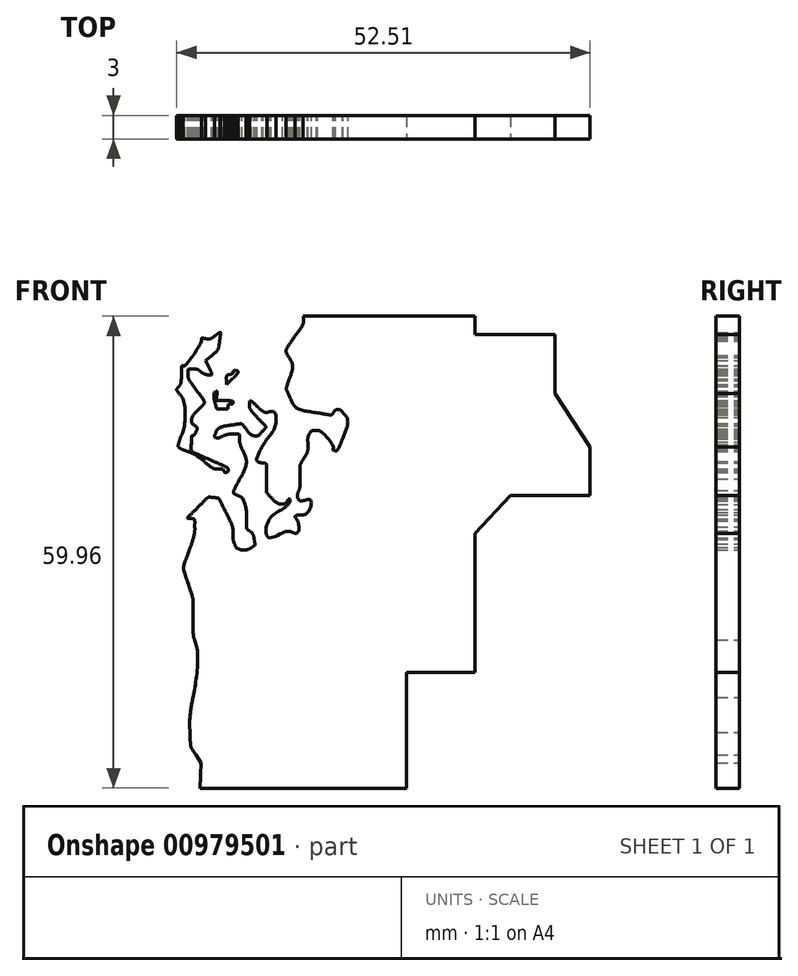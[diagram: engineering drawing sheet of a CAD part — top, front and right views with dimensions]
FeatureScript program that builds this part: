
annotation { "Feature Type Name" : "Feature", "Feature Type Description" : "" }
export const myFeature = defineFeature(function(context is Context, id is Id, definition is map)
    precondition{}
    {
        {
            var Q0;
            Q0=qCreatedBy(makeId("Front.planeOp"),FACE);
            var sketch = newSketch(context, id + "F0", { "sketchPlane" : qUnion([Q0])});
            skLineSegment(sketch, "E0", {"start": v(-32.88, 19.2) * mm, "end": v(-32.1, 20.83) * mm});
            skLineSegment(sketch, "E1", {"start": v(-32.1, 20.83) * mm, "end": v(-32.57, 22.16) * mm});
            skLineSegment(sketch, "E2", {"start": v(-27.5, 16.63) * mm, "end": v(-26.83, 16.28) * mm});
            skLineSegment(sketch, "E3", {"start": v(-26.83, 16.28) * mm, "end": v(-26.97, 16.83) * mm});
            skLineSegment(sketch, "E4", {"start": v(-24.85, 15.67) * mm, "end": v(-25.4, 15.88) * mm});
            skLineSegment(sketch, "E5", {"start": v(-25.4, 15.88) * mm, "end": v(-25.34, 18.4) * mm});
            skLineSegment(sketch, "E6", {"start": v(-1.75, 78.04) * mm, "end": v(-0.2, 79.6) * mm});
            skLineSegment(sketch, "E7", {"start": v(-0.2, 79.6) * mm, "end": v(1.27, 79.6) * mm});
            skLineSegment(sketch, "E8", {"start": v(38.3, 44.26) * mm, "end": v(38.3, 43.17) * mm});
            skLineSegment(sketch, "E9", {"start": v(38.3, 43.17) * mm, "end": v(37.62, 43.24) * mm});
            skLineSegment(sketch, "E10", {"start": v(39.65, -31.25) * mm, "end": v(39.52, -33.83) * mm});
            skLineSegment(sketch, "E11", {"start": v(39.52, -33.83) * mm, "end": v(40.18, -34.42) * mm});
            skLineSegment(sketch, "E12", {"start": v(1.4, 79.08) * mm, "end": v(0.3, 79.22) * mm});
            skLineSegment(sketch, "E13", {"start": v(0.3, 79.22) * mm, "end": v(-1.23, 77.67) * mm});
            skLineSegment(sketch, "E14", {"start": v(-12.51, 69.45) * mm, "end": v(-13.4, 69.45) * mm});
            skLineSegment(sketch, "E15", {"start": v(-13.4, 69.45) * mm, "end": v(-13.27, 67.07) * mm});
            skLineSegment(sketch, "E16", {"start": v(-18.31, 54.9) * mm, "end": v(-18.88, 53.48) * mm});
            skLineSegment(sketch, "E17", {"start": v(-18.88, 53.48) * mm, "end": v(-18.43, 53.1) * mm});
            skLineSegment(sketch, "E18", {"start": v(-20.94, 40.45) * mm, "end": v(-21.55, 40.45) * mm});
            skLineSegment(sketch, "E19", {"start": v(-21.55, 40.45) * mm, "end": v(-21.44, 41.8) * mm});
            skLineSegment(sketch, "E20", {"start": v(-24.47, 43.3) * mm, "end": v(-25.23, 42.61) * mm});
            skLineSegment(sketch, "E21", {"start": v(-25.23, 42.61) * mm, "end": v(-24.8, 41.05) * mm});
            skLineSegment(sketch, "E22", {"start": v(-37.96, -16.18) * mm, "end": v(-37.29, -17.23) * mm});
            skLineSegment(sketch, "E23", {"start": v(-37.29, -17.23) * mm, "end": v(-37.41, -20.41) * mm});
            skLineSegment(sketch, "E24", {"start": v(-30.4, -60.92) * mm, "end": v(-31.42, -62.04) * mm});
            skLineSegment(sketch, "E25", {"start": v(-31.42, -62.04) * mm, "end": v(-30.9, -63.02) * mm});
            skLineSegment(sketch, "E26", {"start": v(-36.35, 33.14) * mm, "end": v(-36.7, 33.88) * mm});
            skLineSegment(sketch, "E27", {"start": v(-36.7, 33.88) * mm, "end": v(-35.92, 34.57) * mm});
            skLineSegment(sketch, "E28", {"start": v(-34.09, 31.43) * mm, "end": v(-34.09, 30.84) * mm});
            skLineSegment(sketch, "E29", {"start": v(-34.09, 30.84) * mm, "end": v(-33.35, 31.56) * mm});
            skFitSpline(sketch, "E30", {"points": [v(-13.45, -80.7) * mm, v(-14.26, -80.4) * mm, v(-15.79, -79.86) * mm, v(-16.84, -79.51) * mm]});
            skFitSpline(sketch, "E31", {"points": [v(-16.84, -79.51) * mm, v(-20.43, -78.33) * mm, v(-20.6, -78.25) * mm, v(-21.55, -77.26) * mm]});
            skFitSpline(sketch, "E32", {"points": [v(-21.55, -77.26) * mm, v(-22.07, -76.72) * mm, v(-23.66, -74.52) * mm, v(-25.09, -72.37) * mm]});
            skFitSpline(sketch, "E33", {"points": [v(-25.09, -72.37) * mm, v(-26.52, -70.21) * mm, v(-28.36, -67.6) * mm, v(-29.19, -66.55) * mm]});
            skFitSpline(sketch, "E34", {"points": [v(-29.19, -66.55) * mm, v(-30.6, -64.76) * mm, v(-31.97, -62.53) * mm, v(-31.97, -62.03) * mm]});
            skFitSpline(sketch, "E35", {"points": [v(-31.97, -62.03) * mm, v(-31.97, -61.91) * mm, v(-31.5, -61.27) * mm, v(-30.92, -60.6) * mm]});
            skFitSpline(sketch, "E36", {"points": [v(-30.92, -60.6) * mm, v(-29.85, -59.39) * mm, v(-29, -57.92) * mm, v(-29, -57.28) * mm]});
            skFitSpline(sketch, "E37", {"points": [v(-29, -57.28) * mm, v(-29, -57.08) * mm, v(-29.34, -56.3) * mm, v(-29.75, -55.53) * mm]});
            skFitSpline(sketch, "E38", {"points": [v(-29.75, -55.53) * mm, v(-30.57, -53.98) * mm, v(-30.63, -53.57) * mm, v(-30.2, -52.72) * mm]});
            skFitSpline(sketch, "E39", {"points": [v(-30.2, -52.72) * mm, v(-29.95, -52.26) * mm, v(-29.92, -51.55) * mm, v(-30.04, -49.29) * mm]});
            skFitSpline(sketch, "E40", {"points": [v(-30.04, -49.29) * mm, v(-30.2, -46.13) * mm, v(-30.12, -46.32) * mm, v(-32.34, -43.6) * mm]});
            skFitSpline(sketch, "E41", {"points": [v(-32.34, -43.6) * mm, v(-32.83, -43) * mm, v(-33.38, -42.01) * mm, v(-33.55, -41.42) * mm]});
            skFitSpline(sketch, "E42", {"points": [v(-33.55, -41.42) * mm, v(-33.73, -40.84) * mm, v(-34.2, -39.94) * mm, v(-34.62, -39.44) * mm]});
            skFitSpline(sketch, "E43", {"points": [v(-34.62, -39.44) * mm, v(-36.03, -37.71) * mm, v(-36.52, -35.97) * mm, v(-35.98, -34.56) * mm]});
            skFitSpline(sketch, "E44", {"points": [v(-35.98, -34.56) * mm, v(-35.86, -34.24) * mm, v(-35.38, -33.57) * mm, v(-34.92, -33.07) * mm]});
            skFitSpline(sketch, "E45", {"points": [v(-34.92, -33.07) * mm, v(-33.97, -32.03) * mm, v(-34, -32.17) * mm, v(-34.37, -30.78) * mm]});
            skFitSpline(sketch, "E46", {"points": [v(-34.37, -30.78) * mm, v(-34.75, -29.38) * mm, v(-35.2, -28.53) * mm, v(-36.46, -26.88) * mm]});
            skFitSpline(sketch, "E47", {"points": [v(-36.46, -26.88) * mm, v(-37.04, -26.13) * mm, v(-37.61, -25.27) * mm, v(-37.73, -24.97) * mm]});
            skFitSpline(sketch, "E48", {"points": [v(-37.73, -24.97) * mm, v(-37.97, -24.39) * mm, v(-38.06, -21.07) * mm, v(-37.9, -18.8) * mm]});
            skFitSpline(sketch, "E49", {"points": [v(-37.9, -18.8) * mm, v(-37.82, -17.55) * mm, v(-37.87, -17.35) * mm, v(-38.39, -16.67) * mm]});
            skFitSpline(sketch, "E50", {"points": [v(-38.39, -16.67) * mm, v(-39.51, -15.19) * mm, v(-39.6, -12.77) * mm, v(-38.72, -7.81) * mm]});
            skFitSpline(sketch, "E51", {"points": [v(-38.72, -7.81) * mm, v(-38.24, -5.14) * mm, v(-38.31, -2.1) * mm, v(-38.87, -1) * mm]});
            skFitSpline(sketch, "E52", {"points": [v(-38.87, -1) * mm, v(-39.1, -0.56) * mm, v(-39.11, -0.29) * mm, v(-38.94, 0.17) * mm]});
            skFitSpline(sketch, "E53", {"points": [v(-38.94, 0.17) * mm, v(-38.62, 1) * mm, v(-38.87, 3.38) * mm, v(-39.5, 5.38) * mm]});
            skFitSpline(sketch, "E54", {"points": [v(-39.5, 5.38) * mm, v(-39.78, 6.29) * mm, v(-40.01, 7.26) * mm, v(-40.01, 7.54) * mm]});
            skFitSpline(sketch, "E55", {"points": [v(-40.01, 7.54) * mm, v(-40.01, 7.83) * mm, v(-39.68, 9.05) * mm, v(-39.27, 10.27) * mm]});
            skFitSpline(sketch, "E56", {"points": [v(-39.27, 10.27) * mm, v(-38.41, 12.85) * mm, v(-38.39, 13.06) * mm, v(-38.96, 13.2) * mm]});
            skFitSpline(sketch, "E57", {"points": [v(-38.96, 13.2) * mm, v(-39.71, 13.4) * mm, v(-39.48, 14.32) * mm, v(-38.38, 15.5) * mm]});
            skFitSpline(sketch, "E58", {"points": [v(-38.38, 15.5) * mm, v(-36.83, 17.16) * mm, v(-35.68, 17.57) * mm, v(-34.74, 16.8) * mm]});
            skFitSpline(sketch, "E59", {"points": [v(-34.74, 16.8) * mm, v(-34.08, 16.26) * mm, v(-32.77, 13.22) * mm, v(-32.66, 11.98) * mm]});
            skFitSpline(sketch, "E60", {"points": [v(-32.66, 11.98) * mm, v(-32.55, 10.86) * mm, v(-32.37, 10.61) * mm, v(-31.6, 10.6) * mm]});
            skFitSpline(sketch, "E61", {"points": [v(-31.6, 10.6) * mm, v(-31, 10.6) * mm, v(-30.96, 11.24) * mm, v(-31.55, 11.77) * mm]});
            skFitSpline(sketch, "E62", {"points": [v(-31.55, 11.77) * mm, v(-31.84, 12.03) * mm, v(-31.97, 12.42) * mm, v(-31.97, 13) * mm]});
            skFitSpline(sketch, "E63", {"points": [v(-31.97, 13) * mm, v(-31.97, 14.32) * mm, v(-32.62, 16.12) * mm, v(-33.18, 16.38) * mm]});
            skFitSpline(sketch, "E64", {"points": [v(-33.18, 16.38) * mm, v(-33.86, 16.69) * mm, v(-33.8, 17.27) * mm, v(-32.88, 19.2) * mm]});
            skFitSpline(sketch, "E65", {"points": [v(-32.57, 22.16) * mm, v(-32.82, 22.9) * mm, v(-33.03, 23.65) * mm, v(-33.03, 23.83) * mm]});
            skFitSpline(sketch, "E66", {"points": [v(-33.03, 23.83) * mm, v(-33.03, 24.1) * mm, v(-33.14, 24.14) * mm, v(-33.5, 24.01) * mm]});
            skFitSpline(sketch, "E67", {"points": [v(-33.5, 24.01) * mm, v(-33.77, 23.92) * mm, v(-34.4, 23.84) * mm, v(-34.93, 23.84) * mm]});
            skFitSpline(sketch, "E68", {"points": [v(-34.93, 23.84) * mm, v(-35.84, 23.83) * mm, v(-35.89, 23.86) * mm, v(-35.95, 24.48) * mm]});
            skFitSpline(sketch, "E69", {"points": [v(-35.95, 24.48) * mm, v(-36.05, 25.55) * mm, v(-34.78, 26.27) * mm, v(-32.78, 26.27) * mm]});
            skFitSpline(sketch, "E70", {"points": [v(-32.78, 26.27) * mm, v(-31.93, 26.27) * mm, v(-31.64, 26.16) * mm, v(-31.1, 25.65) * mm]});
            skFitSpline(sketch, "E71", {"points": [v(-31.1, 25.65) * mm, v(-30.75, 25.3) * mm, v(-30.32, 25.08) * mm, v(-30.15, 25.14) * mm]});
            skFitSpline(sketch, "E72", {"points": [v(-30.15, 25.14) * mm, v(-29.7, 25.31) * mm, v(-29.77, 25.47) * mm, v(-30.7, 26.37) * mm]});
            skFitSpline(sketch, "E73", {"points": [v(-30.7, 26.37) * mm, v(-31.5, 27.15) * mm, v(-31.55, 27.27) * mm, v(-31.55, 28.43) * mm]});
            skFitSpline(sketch, "E74", {"points": [v(-31.55, 28.43) * mm, v(-31.55, 29.6) * mm, v(-31.52, 29.65) * mm, v(-31.02, 29.65) * mm]});
            skFitSpline(sketch, "E75", {"points": [v(-31.02, 29.65) * mm, v(-30.7, 29.65) * mm, v(-30.49, 29.53) * mm, v(-30.49, 29.36) * mm]});
            skFitSpline(sketch, "E76", {"points": [v(-30.49, 29.36) * mm, v(-30.49, 28.94) * mm, v(-28.82, 27.75) * mm, v(-28.24, 27.75) * mm]});
            skFitSpline(sketch, "E77", {"points": [v(-28.24, 27.75) * mm, v(-27.83, 27.75) * mm, v(-27.75, 27.6) * mm, v(-27.62, 26.6) * mm]});
            skFitSpline(sketch, "E78", {"points": [v(-27.62, 26.6) * mm, v(-27.46, 25.26) * mm, v(-27.66, 24.55) * mm, v(-28.57, 23.22) * mm]});
            skFitSpline(sketch, "E79", {"points": [v(-28.57, 23.22) * mm, v(-29.21, 22.29) * mm, v(-29.4, 21.61) * mm, v(-29.02, 21.61) * mm]});
            skFitSpline(sketch, "E80", {"points": [v(-29.02, 21.61) * mm, v(-28.66, 21.61) * mm, v(-28.35, 20.18) * mm, v(-28.49, 19.14) * mm]});
            skFitSpline(sketch, "E81", {"points": [v(-28.49, 19.14) * mm, v(-28.66, 17.84) * mm, v(-28.36, 17.07) * mm, v(-27.5, 16.63) * mm]});
            skFitSpline(sketch, "E82", {"points": [v(-26.97, 16.83) * mm, v(-27.1, 17.33) * mm, v(-27.05, 17.38) * mm, v(-26.5, 17.38) * mm]});
            skFitSpline(sketch, "E83", {"points": [v(-26.5, 17.38) * mm, v(-25.81, 17.38) * mm, v(-25.62, 17.08) * mm, v(-25.62, 16.04) * mm]});
            skFitSpline(sketch, "E84", {"points": [v(-25.62, 16.04) * mm, v(-25.62, 15.5) * mm, v(-25.82, 15.19) * mm, v(-26.56, 14.52) * mm]});
            skFitSpline(sketch, "E85", {"points": [v(-26.56, 14.52) * mm, v(-27.09, 14.05) * mm, v(-27.58, 13.4) * mm, v(-27.66, 13.06) * mm]});
            skFitSpline(sketch, "E86", {"points": [v(-27.66, 13.06) * mm, v(-27.79, 12.49) * mm, v(-27.76, 12.45) * mm, v(-27.3, 12.58) * mm]});
            skFitSpline(sketch, "E87", {"points": [v(-27.3, 12.58) * mm, v(-27.01, 12.65) * mm, v(-26.47, 12.72) * mm, v(-26.09, 12.72) * mm]});
            skFitSpline(sketch, "E88", {"points": [v(-26.09, 12.72) * mm, v(-25.47, 12.72) * mm, v(-25.42, 12.76) * mm, v(-25.61, 13.13) * mm]});
            skFitSpline(sketch, "E89", {"points": [v(-25.61, 13.13) * mm, v(-26.02, 13.88) * mm, v(-25.88, 14.6) * mm, v(-25.31, 14.75) * mm]});
            skFitSpline(sketch, "E90", {"points": [v(-25.31, 14.75) * mm, v(-25.03, 14.82) * mm, v(-24.68, 15.01) * mm, v(-24.55, 15.17) * mm]});
            skFitSpline(sketch, "E91", {"points": [v(-24.55, 15.17) * mm, v(-24.35, 15.4) * mm, v(-24.42, 15.5) * mm, v(-24.85, 15.67) * mm]});
            skFitSpline(sketch, "E92", {"points": [v(-25.34, 18.4) * mm, v(-25.28, 20.49) * mm, v(-25.2, 21.05) * mm, v(-24.84, 21.66) * mm]});
            skFitSpline(sketch, "E93", {"points": [v(-24.84, 21.66) * mm, v(-24.6, 22.07) * mm, v(-24.33, 22.91) * mm, v(-24.25, 23.54) * mm]});
            skFitSpline(sketch, "E94", {"points": [v(-24.25, 23.54) * mm, v(-24.05, 24.98) * mm, v(-23.67, 25.42) * mm, v(-22.64, 25.42) * mm]});
            skFitSpline(sketch, "E95", {"points": [v(-22.64, 25.42) * mm, v(-21.97, 25.42) * mm, v(-21.73, 25.28) * mm, v(-21.09, 24.54) * mm]});
            skFitSpline(sketch, "E96", {"points": [v(-21.09, 24.54) * mm, v(-20.67, 24.05) * mm, v(-20.32, 23.55) * mm, v(-20.32, 23.43) * mm]});
            skFitSpline(sketch, "E97", {"points": [v(-20.32, 23.43) * mm, v(-20.3, 22.93) * mm, v(-19.5, 25.15) * mm, v(-19.5, 25.74) * mm]});
            skFitSpline(sketch, "E98", {"points": [v(-19.5, 25.74) * mm, v(-19.48, 26.68) * mm, v(-19.75, 27) * mm, v(-20.27, 26.68) * mm]});
            skFitSpline(sketch, "E99", {"points": [v(-20.27, 26.68) * mm, v(-20.84, 26.32) * mm, v(-23.7, 26.75) * mm, v(-24.99, 27.38) * mm]});
            skFitSpline(sketch, "E100", {"points": [v(-24.99, 27.38) * mm, v(-26.7, 28.23) * mm, v(-27.27, 29.95) * mm, v(-26.55, 32.07) * mm]});
            skFitSpline(sketch, "E101", {"points": [v(-26.55, 32.07) * mm, v(-26.23, 33) * mm, v(-26.23, 33.13) * mm, v(-26.58, 33.9) * mm]});
            skFitSpline(sketch, "E102", {"points": [v(-26.58, 33.9) * mm, v(-27.04, 34.91) * mm, v(-26.9, 36) * mm, v(-26.2, 36.92) * mm]});
            skFitSpline(sketch, "E103", {"points": [v(-26.2, 36.92) * mm, v(-24.96, 38.54) * mm, v(-24.76, 39.42) * mm, v(-25.3, 40.73) * mm]});
            skFitSpline(sketch, "E104", {"points": [v(-25.3, 40.73) * mm, v(-25.48, 41.15) * mm, v(-25.62, 41.87) * mm, v(-25.62, 42.33) * mm]});
            skFitSpline(sketch, "E105", {"points": [v(-25.62, 42.33) * mm, v(-25.62, 43.02) * mm, v(-25.5, 43.25) * mm, v(-24.99, 43.62) * mm]});
            skFitSpline(sketch, "E106", {"points": [v(-24.99, 43.62) * mm, v(-24.64, 43.87) * mm, v(-24.35, 44.26) * mm, v(-24.35, 44.48) * mm]});
            skFitSpline(sketch, "E107", {"points": [v(-24.35, 44.48) * mm, v(-24.35, 45.6) * mm, v(-22.43, 46.16) * mm, v(-21.62, 45.29) * mm]});
            skFitSpline(sketch, "E108", {"points": [v(-21.62, 45.29) * mm, v(-21.1, 44.74) * mm, v(-20.66, 42.78) * mm, v(-20.82, 41.8) * mm]});
            skFitSpline(sketch, "E109", {"points": [v(-20.82, 41.8) * mm, v(-20.95, 40.98) * mm, v(-20.5, 40.8) * mm, v(-20.12, 41.5) * mm]});
            skFitSpline(sketch, "E110", {"points": [v(-20.12, 41.5) * mm, v(-20, 41.74) * mm, v(-19.7, 41.93) * mm, v(-19.48, 41.93) * mm]});
            skFitSpline(sketch, "E111", {"points": [v(-19.48, 41.93) * mm, v(-19.2, 41.93) * mm, v(-19.03, 42.12) * mm, v(-18.95, 42.51) * mm]});
            skFitSpline(sketch, "E112", {"points": [v(-18.95, 42.51) * mm, v(-18.9, 42.83) * mm, v(-18.75, 43.5) * mm, v(-18.63, 44) * mm]});
            skFitSpline(sketch, "E113", {"points": [v(-18.63, 44) * mm, v(-18.15, 46.1) * mm, v(-18.46, 46.83) * mm, v(-19.95, 47.1) * mm]});
            skFitSpline(sketch, "E114", {"points": [v(-19.95, 47.1) * mm, v(-21.37, 47.35) * mm, v(-21.68, 48.31) * mm, v(-21.02, 50.45) * mm]});
            skFitSpline(sketch, "E115", {"points": [v(-21.02, 50.45) * mm, v(-20.67, 51.58) * mm, v(-20.6, 51.66) * mm, v(-20, 51.67) * mm]});
            skFitSpline(sketch, "E116", {"points": [v(-20, 51.67) * mm, v(-19.64, 51.67) * mm, v(-19.17, 51.8) * mm, v(-18.94, 51.97) * mm]});
            skFitSpline(sketch, "E117", {"points": [v(-18.94, 51.97) * mm, v(-18.56, 52.25) * mm, v(-18.55, 52.28) * mm, v(-18.9, 52.67) * mm]});
            skFitSpline(sketch, "E118", {"points": [v(-18.9, 52.67) * mm, v(-19.36, 53.18) * mm, v(-19.37, 53.99) * mm, v(-18.93, 55) * mm]});
            skFitSpline(sketch, "E119", {"points": [v(-18.93, 55) * mm, v(-18.26, 56.57) * mm, v(-18.22, 56.96) * mm, v(-18.55, 58.71) * mm]});
            skFitSpline(sketch, "E120", {"points": [v(-18.55, 58.71) * mm, v(-19.05, 61.35) * mm, v(-18.66, 63.1) * mm, v(-17.57, 63.1) * mm]});
            skFitSpline(sketch, "E121", {"points": [v(-17.57, 63.1) * mm, v(-17.13, 63.1) * mm, v(-16.93, 62.86) * mm, v(-16.62, 61.94) * mm]});
            skFitSpline(sketch, "E122", {"points": [v(-16.62, 61.94) * mm, v(-16.19, 60.62) * mm, v(-15.25, 61.36) * mm, v(-15.25, 63.03) * mm]});
            skFitSpline(sketch, "E123", {"points": [v(-15.25, 63.03) * mm, v(-15.25, 63.72) * mm, v(-15.21, 63.77) * mm, v(-14.72, 63.65) * mm]});
            skFitSpline(sketch, "E124", {"points": [v(-14.72, 63.65) * mm, v(-13.88, 63.44) * mm, v(-13.7, 64.21) * mm, v(-13.86, 67.25) * mm]});
            skFitSpline(sketch, "E125", {"points": [v(-13.86, 67.25) * mm, v(-14.01, 70.15) * mm, v(-14.06, 70.07) * mm, v(-12.21, 70.08) * mm]});
            skFitSpline(sketch, "E126", {"points": [v(-12.21, 70.08) * mm, v(-11.52, 70.08) * mm, v(-11.25, 70.23) * mm, v(-10.4, 71.12) * mm]});
            skFitSpline(sketch, "E127", {"points": [v(-10.4, 71.12) * mm, v(-9.38, 72.18) * mm, v(-9.03, 72.34) * mm, v(-6.52, 72.84) * mm]});
            skFitSpline(sketch, "E128", {"points": [v(-6.52, 72.84) * mm, v(-4.93, 73.15) * mm, v(-4.21, 73.78) * mm, v(-3.7, 75.27) * mm]});
            skFitSpline(sketch, "E129", {"points": [v(-3.7, 75.27) * mm, v(-3.38, 76.2) * mm, v(-2.96, 76.8) * mm, v(-1.75, 78.04) * mm]});
            skFitSpline(sketch, "E130", {"points": [v(1.27, 79.6) * mm, v(2.66, 79.6) * mm, v(2.79, 79.65) * mm, v(3.57, 80.36) * mm]});
            skFitSpline(sketch, "E131", {"points": [v(3.57, 80.36) * mm, v(4.72, 81.4) * mm, v(5.62, 81.51) * mm, v(6.84, 80.8) * mm]});
            skFitSpline(sketch, "E132", {"points": [v(6.84, 80.8) * mm, v(7.4, 80.48) * mm, v(8.11, 80.24) * mm, v(8.56, 80.24) * mm]});
            skFitSpline(sketch, "E133", {"points": [v(8.56, 80.24) * mm, v(9.65, 80.24) * mm, v(10.66, 79.76) * mm, v(12.03, 78.58) * mm]});
            skFitSpline(sketch, "E134", {"points": [v(12.03, 78.58) * mm, v(12.68, 78.02) * mm, v(13.76, 77.21) * mm, v(14.43, 76.8) * mm]});
            skFitSpline(sketch, "E135", {"points": [v(14.43, 76.8) * mm, v(16.07, 75.75) * mm, v(16.3, 75.23) * mm, v(16.26, 72.68) * mm]});
            skFitSpline(sketch, "E136", {"points": [v(16.26, 72.68) * mm, v(16.21, 70.3) * mm, v(16.3, 70.06) * mm, v(17.99, 67.97) * mm]});
            skFitSpline(sketch, "E137", {"points": [v(17.99, 67.97) * mm, v(19.34, 66.28) * mm, v(19.58, 65.73) * mm, v(19.78, 63.84) * mm]});
            skFitSpline(sketch, "E138", {"points": [v(19.78, 63.84) * mm, v(19.97, 61.97) * mm, v(20.1, 61.75) * mm, v(21.2, 61.28) * mm]});
            skFitSpline(sketch, "E139", {"points": [v(21.2, 61.28) * mm, v(21.95, 60.97) * mm, v(22.77, 60.9) * mm, v(25.95, 60.87) * mm]});
            skFitSpline(sketch, "E140", {"points": [v(25.95, 60.87) * mm, v(29.47, 60.83) * mm, v(29.87, 60.8) * mm, v(30.78, 60.35) * mm]});
            skFitSpline(sketch, "E141", {"points": [v(30.78, 60.35) * mm, v(31.33, 60.09) * mm, v(31.82, 59.71) * mm, v(31.88, 59.53) * mm]});
            skFitSpline(sketch, "E142", {"points": [v(31.88, 59.53) * mm, v(32.1, 58.78) * mm, v(32.32, 58.58) * mm, v(33.34, 58.19) * mm]});
            skFitSpline(sketch, "E143", {"points": [v(33.34, 58.19) * mm, v(35, 57.54) * mm, v(35.47, 56.96) * mm, v(35.61, 55.41) * mm]});
            skFitSpline(sketch, "E144", {"points": [v(35.61, 55.41) * mm, v(35.68, 54.7) * mm, v(35.93, 53.67) * mm, v(36.17, 53.15) * mm]});
            skFitSpline(sketch, "E145", {"points": [v(36.17, 53.15) * mm, v(36.4, 52.63) * mm, v(36.6, 51.94) * mm, v(36.6, 51.62) * mm]});
            skFitSpline(sketch, "E146", {"points": [v(36.6, 51.62) * mm, v(36.6, 51.3) * mm, v(36.8, 50.55) * mm, v(37.02, 49.93) * mm]});
            skFitSpline(sketch, "E147", {"points": [v(37.02, 49.93) * mm, v(37.7, 48.08) * mm, v(38.3, 45.42) * mm, v(38.3, 44.26) * mm]});
            skFitSpline(sketch, "E148", {"points": [v(37.62, 43.24) * mm, v(36.87, 43.31) * mm, v(36.86, 43.33) * mm, v(36.05, 46.9) * mm]});
            skFitSpline(sketch, "E149", {"points": [v(36.05, 46.9) * mm, v(35.75, 48.23) * mm, v(35.65, 48.45) * mm, v(35.6, 47.92) * mm]});
            skFitSpline(sketch, "E150", {"points": [v(35.6, 47.92) * mm, v(35.56, 47.55) * mm, v(35.72, 46.61) * mm, v(35.96, 45.84) * mm]});
            skFitSpline(sketch, "E151", {"points": [v(35.96, 45.84) * mm, v(36.2, 45.06) * mm, v(36.4, 44.16) * mm, v(36.4, 43.83) * mm]});
            skFitSpline(sketch, "E152", {"points": [v(36.4, 43.83) * mm, v(36.4, 42.72) * mm, v(36.23, 42.57) * mm, v(35.04, 42.57) * mm]});
            skFitSpline(sketch, "E153", {"points": [v(35.04, 42.57) * mm, v(34.35, 42.57) * mm, v(33.78, 42.44) * mm, v(33.53, 42.23) * mm]});
            skFitSpline(sketch, "E154", {"points": [v(33.53, 42.23) * mm, v(33.14, 41.92) * mm, v(33.15, 41.9) * mm, v(33.78, 42.01) * mm]});
            skFitSpline(sketch, "E155", {"points": [v(33.78, 42.01) * mm, v(34.37, 42.1) * mm, v(34.48, 42.05) * mm, v(34.7, 41.5) * mm]});
            skFitSpline(sketch, "E156", {"points": [v(34.7, 41.5) * mm, v(35.23, 40.23) * mm, v(34.46, 39.89) * mm, v(32.77, 40.66) * mm]});
            skFitSpline(sketch, "E157", {"points": [v(32.77, 40.66) * mm, v(30, 41.91) * mm, v(30.46, 40.26) * mm, v(33.3, 38.77) * mm]});
            skFitSpline(sketch, "E158", {"points": [v(33.3, 38.77) * mm, v(34.7, 38.04) * mm, v(35.03, 37.98) * mm, v(35.2, 38.44) * mm]});
            skFitSpline(sketch, "E159", {"points": [v(35.2, 38.44) * mm, v(35.4, 38.97) * mm, v(36.94, 38.86) * mm, v(37.34, 38.29) * mm]});
            skFitSpline(sketch, "E160", {"points": [v(37.34, 38.29) * mm, v(37.8, 37.64) * mm, v(37.75, 36.5) * mm, v(37.25, 35.69) * mm]});
            skFitSpline(sketch, "E161", {"points": [v(37.25, 35.69) * mm, v(37.01, 35.31) * mm, v(36.68, 34.6) * mm, v(36.5, 34.09) * mm]});
            skFitSpline(sketch, "E162", {"points": [v(36.5, 34.09) * mm, v(36.07, 32.87) * mm, v(35.62, 32.4) * mm, v(34.86, 32.4) * mm]});
            skFitSpline(sketch, "E163", {"points": [v(34.86, 32.4) * mm, v(34.06, 32.4) * mm, v(32.85, 32.98) * mm, v(32.57, 33.5) * mm]});
            skFitSpline(sketch, "E164", {"points": [v(32.57, 33.5) * mm, v(32.35, 33.9) * mm, v(32.37, 33.91) * mm, v(33.4, 34.23) * mm]});
            skFitSpline(sketch, "E165", {"points": [v(33.4, 34.23) * mm, v(33.55, 34.27) * mm, v(33.64, 34.43) * mm, v(33.6, 34.58) * mm]});
            skFitSpline(sketch, "E166", {"points": [v(33.6, 34.58) * mm, v(33.47, 34.97) * mm, v(32.1, 35.02) * mm, v(31.26, 34.66) * mm]});
            skFitSpline(sketch, "E167", {"points": [v(31.26, 34.66) * mm, v(30.63, 34.4) * mm, v(30.54, 34.27) * mm, v(30.63, 33.8) * mm]});
            skFitSpline(sketch, "E168", {"points": [v(30.63, 33.8) * mm, v(30.71, 33.37) * mm, v(30.83, 33.27) * mm, v(31.13, 33.37) * mm]});
            skFitSpline(sketch, "E169", {"points": [v(31.13, 33.37) * mm, v(31.68, 33.54) * mm, v(31.8, 33.13) * mm, v(31.57, 31.7) * mm]});
            skFitSpline(sketch, "E170", {"points": [v(31.57, 31.7) * mm, v(31.47, 31.04) * mm, v(31.4, 30.5) * mm, v(31.43, 30.5) * mm]});
            skFitSpline(sketch, "E171", {"points": [v(31.43, 30.5) * mm, v(31.46, 30.5) * mm, v(31.82, 30.65) * mm, v(32.25, 30.82) * mm]});
            skFitSpline(sketch, "E172", {"points": [v(32.25, 30.82) * mm, v(33.01, 31.14) * mm, v(33.02, 31.14) * mm, v(33.26, 30.56) * mm]});
            skFitSpline(sketch, "E173", {"points": [v(33.26, 30.56) * mm, v(33.39, 30.24) * mm, v(33.5, 29.43) * mm, v(33.52, 28.77) * mm]});
            skFitSpline(sketch, "E174", {"points": [v(33.52, 28.77) * mm, v(33.55, 27.14) * mm, v(33.03, 26.57) * mm, v(31.4, 26.43) * mm]});
            skFitSpline(sketch, "E175", {"points": [v(31.4, 26.43) * mm, v(29.99, 26.32) * mm, v(29.27, 25.83) * mm, v(28.59, 24.5) * mm]});
            skFitSpline(sketch, "E176", {"points": [v(28.59, 24.5) * mm, v(28.09, 23.52) * mm, v(28.09, 23.5) * mm, v(28.46, 22.8) * mm]});
            skFitSpline(sketch, "E177", {"points": [v(28.46, 22.8) * mm, v(29.02, 21.76) * mm, v(28.8, 20.5) * mm, v(27.76, 18.77) * mm]});
            skFitSpline(sketch, "E178", {"points": [v(27.76, 18.77) * mm, v(26.26, 16.28) * mm, v(26.34, 15.6) * mm, v(28.5, 12.89) * mm]});
            skFitSpline(sketch, "E179", {"points": [v(28.5, 12.89) * mm, v(30.07, 10.9) * mm, v(30.64, 9.85) * mm, v(31.32, 7.7) * mm]});
            skFitSpline(sketch, "E180", {"points": [v(31.32, 7.7) * mm, v(31.79, 6.2) * mm, v(31.8, 6.14) * mm, v(31.41, 5.73) * mm]});
            skFitSpline(sketch, "E181", {"points": [v(31.41, 5.73) * mm, v(31.08, 5.36) * mm, v(31.06, 5.2) * mm, v(31.28, 4.6) * mm]});
            skFitSpline(sketch, "E182", {"points": [v(31.28, 4.6) * mm, v(31.65, 3.58) * mm, v(31.59, 2.92) * mm, v(31, 1.59) * mm]});
            skFitSpline(sketch, "E183", {"points": [v(31, 1.59) * mm, v(30.4, 0.22) * mm, v(30.37, 0) * mm, v(30.73, -0.98) * mm]});
            skFitSpline(sketch, "E184", {"points": [v(30.73, -0.98) * mm, v(30.96, -1.6) * mm, v(30.93, -1.79) * mm, v(30.48, -2.62) * mm]});
            skFitSpline(sketch, "E185", {"points": [v(30.48, -2.62) * mm, v(29.76, -3.92) * mm, v(30.03, -4.4) * mm, v(31.97, -5.39) * mm]});
            skFitSpline(sketch, "E186", {"points": [v(31.97, -5.39) * mm, v(33.32, -6.07) * mm, v(33.55, -6.12) * mm, v(34.1, -5.9) * mm]});
            skFitSpline(sketch, "E187", {"points": [v(34.1, -5.9) * mm, v(34.89, -5.57) * mm, v(35.48, -5.74) * mm, v(36.67, -6.64) * mm]});
            skFitSpline(sketch, "E188", {"points": [v(36.67, -6.64) * mm, v(37.21, -7.06) * mm, v(37.94, -7.45) * mm, v(38.28, -7.52) * mm]});
            skFitSpline(sketch, "E189", {"points": [v(38.28, -7.52) * mm, v(38.74, -7.61) * mm, v(38.97, -7.82) * mm, v(39.14, -8.29) * mm]});
            skFitSpline(sketch, "E190", {"points": [v(39.14, -8.29) * mm, v(39.46, -9.22) * mm, v(39.43, -9.36) * mm, v(38.73, -10.24) * mm]});
            skFitSpline(sketch, "E191", {"points": [v(38.73, -10.24) * mm, v(37.95, -11.22) * mm, v(37.9, -12.13) * mm, v(38.57, -13.12) * mm]});
            skFitSpline(sketch, "E192", {"points": [v(38.57, -13.12) * mm, v(38.94, -13.67) * mm, v(39.23, -13.86) * mm, v(39.79, -13.91) * mm]});
            skFitSpline(sketch, "E193", {"points": [v(39.79, -13.91) * mm, v(40.2, -13.95) * mm, v(40.6, -14.1) * mm, v(40.68, -14.23) * mm]});
            skFitSpline(sketch, "E194", {"points": [v(40.68, -14.23) * mm, v(40.98, -14.7) * mm, v(40.84, -15.58) * mm, v(40.4, -15.98) * mm]});
            skFitSpline(sketch, "E195", {"points": [v(40.4, -15.98) * mm, v(40.04, -16.3) * mm, v(39.97, -16.56) * mm, v(40.05, -17.26) * mm]});
            skFitSpline(sketch, "E196", {"points": [v(40.05, -17.26) * mm, v(40.14, -18.03) * mm, v(40.09, -18.17) * mm, v(39.65, -18.37) * mm]});
            skFitSpline(sketch, "E197", {"points": [v(39.65, -18.37) * mm, v(39.06, -18.64) * mm, v(39.03, -18.9) * mm, v(39.5, -20) * mm]});
            skFitSpline(sketch, "E198", {"points": [v(39.5, -20) * mm, v(39.77, -20.67) * mm, v(39.83, -21.57) * mm, v(39.81, -24.74) * mm]});
            skFitSpline(sketch, "E199", {"points": [v(39.81, -24.74) * mm, v(39.8, -26.9) * mm, v(39.73, -29.82) * mm, v(39.65, -31.25) * mm]});
            skFitSpline(sketch, "E200", {"points": [v(40.18, -34.42) * mm, v(40.54, -34.74) * mm, v(40.84, -35.18) * mm, v(40.84, -35.41) * mm]});
            skFitSpline(sketch, "E201", {"points": [v(40.84, -35.41) * mm, v(40.84, -36.27) * mm, v(39.96, -37.65) * mm, v(38.92, -38.41) * mm]});
            skFitSpline(sketch, "E202", {"points": [v(38.92, -38.41) * mm, v(37.63, -39.36) * mm, v(37.28, -40) * mm, v(37.05, -41.89) * mm]});
            skFitSpline(sketch, "E203", {"points": [v(37.05, -41.89) * mm, v(36.94, -42.7) * mm, v(36.66, -43.77) * mm, v(36.42, -44.27) * mm]});
            skFitSpline(sketch, "E204", {"points": [v(36.42, -44.27) * mm, v(35.96, -45.22) * mm, v(33.78, -47.87) * mm, v(31.3, -50.5) * mm]});
            skFitSpline(sketch, "E205", {"points": [v(31.3, -50.5) * mm, v(29.02, -52.92) * mm, v(27.8, -55.66) * mm, v(27.2, -59.77) * mm]});
            skFitSpline(sketch, "E206", {"points": [v(27.2, -59.77) * mm, v(26.85, -62.13) * mm, v(26.75, -62.37) * mm, v(25.14, -65) * mm]});
            skFitSpline(sketch, "E207", {"points": [v(25.14, -65) * mm, v(24.58, -65.91) * mm, v(24.35, -66.6) * mm, v(24.16, -67.9) * mm]});
            skFitSpline(sketch, "E208", {"points": [v(24.16, -67.9) * mm, v(23.88, -69.93) * mm, v(23.36, -71.03) * mm, v(22.29, -71.92) * mm]});
            skFitSpline(sketch, "E209", {"points": [v(22.29, -71.92) * mm, v(21.43, -72.63) * mm, v(19.94, -73.22) * mm, v(19, -73.22) * mm]});
            skFitSpline(sketch, "E210", {"points": [v(19, -73.22) * mm, v(18.6, -73.22) * mm, v(18.4, -73.32) * mm, v(18.4, -73.56) * mm]});
            skFitSpline(sketch, "E211", {"points": [v(18.4, -73.56) * mm, v(18.4, -73.75) * mm, v(18.21, -74.22) * mm, v(17.97, -74.6) * mm]});
            skFitSpline(sketch, "E212", {"points": [v(17.97, -74.6) * mm, v(17.57, -75.26) * mm, v(17.56, -75.35) * mm, v(17.87, -76.08) * mm]});
            skFitSpline(sketch, "E213", {"points": [v(17.87, -76.08) * mm, v(18.34, -77.22) * mm, v(18.3, -77.38) * mm, v(17.14, -78.58) * mm]});
            skFitSpline(sketch, "E214", {"points": [v(17.14, -78.58) * mm, v(16.56, -79.18) * mm, v(15.87, -79.93) * mm, v(15.6, -80.25) * mm]});
            skFitSpline(sketch, "E215", {"points": [v(15.6, -80.25) * mm, v(15.34, -80.56) * mm, v(14.86, -80.88) * mm, v(14.54, -80.96) * mm]});
            skFitSpline(sketch, "E216", {"points": [v(14.54, -80.96) * mm, v(14.03, -81.08) * mm, v(13.96, -81.03) * mm, v(13.96, -80.56) * mm]});
            skFitSpline(sketch, "E217", {"points": [v(13.96, -80.56) * mm, v(13.96, -80.25) * mm, v(13.75, -79.86) * mm, v(13.47, -79.63) * mm]});
            skFitSpline(sketch, "E218", {"points": [v(13.47, -79.63) * mm, v(12.33, -78.73) * mm, v(12.3, -77.45) * mm, v(13.44, -77.45) * mm]});
            skFitSpline(sketch, "E219", {"points": [v(13.44, -77.45) * mm, v(14.2, -77.45) * mm, v(15.11, -76) * mm, v(14.94, -75.07) * mm]});
            skFitSpline(sketch, "E220", {"points": [v(14.94, -75.07) * mm, v(14.87, -74.7) * mm, v(14.75, -74.02) * mm, v(14.67, -73.57) * mm]});
            skFitSpline(sketch, "E221", {"points": [v(14.67, -73.57) * mm, v(14.58, -73.02) * mm, v(14.45, -72.8) * mm, v(14.25, -72.88) * mm]});
            skFitSpline(sketch, "E222", {"points": [v(14.25, -72.88) * mm, v(14.1, -72.94) * mm, v(13.13, -72.88) * mm, v(12.11, -72.76) * mm]});
            skFitSpline(sketch, "E223", {"points": [v(12.11, -72.76) * mm, v(10.8, -72.6) * mm, v(10.12, -72.4) * mm, v(9.8, -72.1) * mm]});
            skFitSpline(sketch, "E224", {"points": [v(9.8, -72.1) * mm, v(9.32, -71.67) * mm, v(8.88, -71.75) * mm, v(8.88, -72.28) * mm]});
            skFitSpline(sketch, "E225", {"points": [v(8.88, -72.28) * mm, v(8.88, -72.66) * mm, v(8.5, -72.65) * mm, v(7.82, -72.26) * mm]});
            skFitSpline(sketch, "E226", {"points": [v(7.82, -72.26) * mm, v(7.11, -71.86) * mm, v(5.83, -71.87) * mm, v(4.94, -72.29) * mm]});
            skFitSpline(sketch, "E227", {"points": [v(4.94, -72.29) * mm, v(4.16, -72.66) * mm, v(4.18, -72.61) * mm, v(4.14, -74.27) * mm]});
            skFitSpline(sketch, "E228", {"points": [v(4.14, -74.27) * mm, v(4.12, -75.43) * mm, v(4.11, -75.44) * mm, v(3.17, -75.91) * mm]});
            skFitSpline(sketch, "E229", {"points": [v(3.17, -75.91) * mm, v(2.65, -76.18) * mm, v(1.84, -76.77) * mm, v(1.36, -77.24) * mm]});
            skFitSpline(sketch, "E230", {"points": [v(1.36, -77.24) * mm, v(0.68, -77.91) * mm, v(-0.19, -78.37) * mm, v(-2.67, -79.37) * mm]});
            skFitSpline(sketch, "E231", {"points": [v(-2.67, -79.37) * mm, v(-6.5, -80.92) * mm, v(-7.82, -81.25) * mm, v(-10.17, -81.25) * mm]});
            skFitSpline(sketch, "E232", {"points": [v(-10.17, -81.25) * mm, v(-11.59, -81.25) * mm, v(-12.28, -81.13) * mm, v(-13.45, -80.7) * mm]});
            skFitSpline(sketch, "E233", {"points": [v(-6.84, -80.3) * mm, v(-6.29, -80.14) * mm, v(-4.56, -79.5) * mm, v(-3, -78.88) * mm]});
            skFitSpline(sketch, "E234", {"points": [v(-3, -78.88) * mm, v(-0.66, -77.96) * mm, v(0.05, -77.57) * mm, v(1.08, -76.65) * mm]});
            skFitSpline(sketch, "E235", {"points": [v(1.08, -76.65) * mm, v(1.77, -76.04) * mm, v(2.46, -75.54) * mm, v(2.62, -75.54) * mm]});
            skFitSpline(sketch, "E236", {"points": [v(2.62, -75.54) * mm, v(2.78, -75.54) * mm, v(3.12, -75.37) * mm, v(3.38, -75.16) * mm]});
            skFitSpline(sketch, "E237", {"points": [v(3.38, -75.16) * mm, v(3.8, -74.81) * mm, v(3.83, -74.72) * mm, v(3.59, -73.93) * mm]});
            skFitSpline(sketch, "E238", {"points": [v(3.59, -73.93) * mm, v(3.4, -73.28) * mm, v(3.39, -72.96) * mm, v(3.57, -72.61) * mm]});
            skFitSpline(sketch, "E239", {"points": [v(3.57, -72.61) * mm, v(4.07, -71.69) * mm, v(6.12, -71.11) * mm, v(7.53, -71.5) * mm]});
            skFitSpline(sketch, "E240", {"points": [v(7.53, -71.5) * mm, v(8.17, -71.68) * mm, v(8.4, -71.66) * mm, v(8.68, -71.41) * mm]});
            skFitSpline(sketch, "E241", {"points": [v(8.68, -71.41) * mm, v(9.15, -70.98) * mm, v(9.64, -71.02) * mm, v(10.13, -71.54) * mm]});
            skFitSpline(sketch, "E242", {"points": [v(10.13, -71.54) * mm, v(10.44, -71.88) * mm, v(10.95, -72.03) * mm, v(12.2, -72.17) * mm]});
            skFitSpline(sketch, "E243", {"points": [v(12.2, -72.17) * mm, v(13.1, -72.28) * mm, v(14, -72.32) * mm, v(14.17, -72.26) * mm]});
            skFitSpline(sketch, "E244", {"points": [v(14.17, -72.26) * mm, v(14.75, -72.09) * mm, v(15.04, -72.5) * mm, v(15.33, -73.91) * mm]});
            skFitSpline(sketch, "E245", {"points": [v(15.33, -73.91) * mm, v(15.54, -74.89) * mm, v(15.57, -75.53) * mm, v(15.43, -76.04) * mm]});
            skFitSpline(sketch, "E246", {"points": [v(15.43, -76.04) * mm, v(15.14, -77.06) * mm, v(14.45, -77.87) * mm, v(13.85, -77.87) * mm]});
            skFitSpline(sketch, "E247", {"points": [v(13.85, -77.87) * mm, v(13.06, -77.87) * mm, v(13.01, -78.27) * mm, v(13.7, -79) * mm]});
            skFitSpline(sketch, "E248", {"points": [v(13.7, -79) * mm, v(14.06, -79.37) * mm, v(14.38, -79.86) * mm, v(14.43, -80.1) * mm]});
            skFitSpline(sketch, "E249", {"points": [v(14.43, -80.1) * mm, v(14.5, -80.48) * mm, v(14.55, -80.47) * mm, v(15.03, -79.9) * mm]});
            skFitSpline(sketch, "E250", {"points": [v(15.03, -79.9) * mm, v(15.31, -79.57) * mm, v(16.02, -78.83) * mm, v(16.6, -78.28) * mm]});
            skFitSpline(sketch, "E251", {"points": [v(16.6, -78.28) * mm, v(17.64, -77.28) * mm, v(17.65, -77.26) * mm, v(17.4, -76.55) * mm]});
            skFitSpline(sketch, "E252", {"points": [v(17.4, -76.55) * mm, v(17.05, -75.6) * mm, v(17.07, -74.87) * mm, v(17.45, -74.37) * mm]});
            skFitSpline(sketch, "E253", {"points": [v(17.45, -74.37) * mm, v(17.62, -74.14) * mm, v(17.76, -73.7) * mm, v(17.76, -73.4) * mm]});
            skFitSpline(sketch, "E254", {"points": [v(17.76, -73.4) * mm, v(17.77, -72.89) * mm, v(17.86, -72.83) * mm, v(18.88, -72.7) * mm]});
            skFitSpline(sketch, "E255", {"points": [v(18.88, -72.7) * mm, v(19.5, -72.62) * mm, v(20.47, -72.3) * mm, v(21.04, -71.99) * mm]});
            skFitSpline(sketch, "E256", {"points": [v(21.04, -71.99) * mm, v(22.45, -71.22) * mm, v(23.22, -70.08) * mm, v(23.5, -68.35) * mm]});
            skFitSpline(sketch, "E257", {"points": [v(23.5, -68.35) * mm, v(23.9, -65.9) * mm, v(24.16, -65.2) * mm, v(25.1, -63.87) * mm]});
            skFitSpline(sketch, "E258", {"points": [v(25.1, -63.87) * mm, v(26.18, -62.33) * mm, v(26.35, -61.85) * mm, v(26.67, -59.46) * mm]});
            skFitSpline(sketch, "E259", {"points": [v(26.67, -59.46) * mm, v(26.98, -57.13) * mm, v(27.93, -54.18) * mm, v(28.89, -52.58) * mm]});
            skFitSpline(sketch, "E260", {"points": [v(28.89, -52.58) * mm, v(29.3, -51.88) * mm, v(30.25, -50.69) * mm, v(31, -49.93) * mm]});
            skFitSpline(sketch, "E261", {"points": [v(31, -49.93) * mm, v(33.26, -47.61) * mm, v(35.36, -45.01) * mm, v(35.9, -43.88) * mm]});
            skFitSpline(sketch, "E262", {"points": [v(35.9, -43.88) * mm, v(36.17, -43.28) * mm, v(36.49, -42.11) * mm, v(36.6, -41.27) * mm]});
            skFitSpline(sketch, "E263", {"points": [v(36.6, -41.27) * mm, v(36.81, -39.5) * mm, v(37.06, -39.06) * mm, v(38.37, -38.07) * mm]});
            skFitSpline(sketch, "E264", {"points": [v(38.37, -38.07) * mm, v(39.26, -37.4) * mm, v(40.2, -36.1) * mm, v(40.2, -35.57) * mm]});
            skFitSpline(sketch, "E265", {"points": [v(40.2, -35.57) * mm, v(40.2, -35.45) * mm, v(39.98, -35.11) * mm, v(39.7, -34.83) * mm]});
            skFitSpline(sketch, "E266", {"points": [v(39.7, -34.83) * mm, v(38.98, -34.12) * mm, v(38.86, -33.18) * mm, v(39.13, -30.68) * mm]});
            skFitSpline(sketch, "E267", {"points": [v(39.13, -30.68) * mm, v(39.26, -29.5) * mm, v(39.36, -26.93) * mm, v(39.36, -24.95) * mm]});
            skFitSpline(sketch, "E268", {"points": [v(39.36, -24.95) * mm, v(39.36, -21.87) * mm, v(39.3, -21.22) * mm, v(38.94, -20.3) * mm]});
            skFitSpline(sketch, "E269", {"points": [v(38.94, -20.3) * mm, v(38.39, -18.9) * mm, v(38.4, -18.51) * mm, v(39.04, -18) * mm]});
            skFitSpline(sketch, "E270", {"points": [v(39.04, -18) * mm, v(39.45, -17.69) * mm, v(39.57, -17.4) * mm, v(39.57, -16.76) * mm]});
            skFitSpline(sketch, "E271", {"points": [v(39.57, -16.76) * mm, v(39.57, -16.2) * mm, v(39.7, -15.8) * mm, v(39.97, -15.56) * mm]});
            skFitSpline(sketch, "E272", {"points": [v(39.97, -15.56) * mm, v(40.59, -15) * mm, v(40.32, -14.37) * mm, v(39.46, -14.37) * mm]});
            skFitSpline(sketch, "E273", {"points": [v(39.46, -14.37) * mm, v(38.38, -14.37) * mm, v(37.67, -13.4) * mm, v(37.67, -11.9) * mm]});
            skFitSpline(sketch, "E274", {"points": [v(37.67, -11.9) * mm, v(37.67, -10.72) * mm, v(37.93, -9.95) * mm, v(38.44, -9.65) * mm]});
            skFitSpline(sketch, "E275", {"points": [v(38.44, -9.65) * mm, v(39.04, -9.3) * mm, v(38.7, -8.02) * mm, v(38, -8.02) * mm]});
            skFitSpline(sketch, "E276", {"points": [v(38, -8.02) * mm, v(37.74, -8.02) * mm, v(37, -7.64) * mm, v(36.34, -7.18) * mm]});
            skFitSpline(sketch, "E277", {"points": [v(36.34, -7.18) * mm, v(35.18, -6.34) * mm, v(34.43, -6.12) * mm, v(34.18, -6.54) * mm]});
            skFitSpline(sketch, "E278", {"points": [v(34.18, -6.54) * mm, v(34.1, -6.66) * mm, v(33.87, -6.75) * mm, v(33.65, -6.75) * mm]});
            skFitSpline(sketch, "E279", {"points": [v(33.65, -6.75) * mm, v(33.07, -6.75) * mm, v(30.08, -5.09) * mm, v(29.83, -4.63) * mm]});
            skFitSpline(sketch, "E280", {"points": [v(29.83, -4.63) * mm, v(29.5, -4) * mm, v(29.6, -2.89) * mm, v(30.04, -2.22) * mm]});
            skFitSpline(sketch, "E281", {"points": [v(30.04, -2.22) * mm, v(30.4, -1.66) * mm, v(30.41, -1.54) * mm, v(30.14, -1.01) * mm]});
            skFitSpline(sketch, "E282", {"points": [v(30.14, -1.01) * mm, v(29.71, -0.19) * mm, v(29.76, 0.38) * mm, v(30.37, 1.68) * mm]});
            skFitSpline(sketch, "E283", {"points": [v(30.37, 1.68) * mm, v(30.96, 2.95) * mm, v(31, 3.5) * mm, v(30.65, 4.7) * mm]});
            skFitSpline(sketch, "E284", {"points": [v(30.65, 4.7) * mm, v(30.44, 5.4) * mm, v(30.46, 5.58) * mm, v(30.78, 5.93) * mm]});
            skFitSpline(sketch, "E285", {"points": [v(30.78, 5.93) * mm, v(31.13, 6.33) * mm, v(31.13, 6.4) * mm, v(30.68, 7.79) * mm]});
            skFitSpline(sketch, "E286", {"points": [v(30.68, 7.79) * mm, v(30.01, 9.8) * mm, v(29.64, 10.47) * mm, v(28.1, 12.43) * mm]});
            skFitSpline(sketch, "E287", {"points": [v(28.1, 12.43) * mm, v(27.35, 13.37) * mm, v(26.61, 14.44) * mm, v(26.46, 14.8) * mm]});
            skFitSpline(sketch, "E288", {"points": [v(26.46, 14.8) * mm, v(26, 15.95) * mm, v(26.28, 17.5) * mm, v(27.26, 19.16) * mm]});
            skFitSpline(sketch, "E289", {"points": [v(27.26, 19.16) * mm, v(28.4, 21.1) * mm, v(28.53, 21.7) * mm, v(27.93, 22.5) * mm]});
            skFitSpline(sketch, "E290", {"points": [v(27.93, 22.5) * mm, v(27.4, 23.23) * mm, v(27.46, 23.77) * mm, v(28.28, 25.17) * mm]});
            skFitSpline(sketch, "E291", {"points": [v(28.28, 25.17) * mm, v(28.94, 26.3) * mm, v(29.89, 26.9) * mm, v(31.02, 26.9) * mm]});
            skFitSpline(sketch, "E292", {"points": [v(31.02, 26.9) * mm, v(31.6, 26.9) * mm, v(32.1, 27.06) * mm, v(32.48, 27.36) * mm]});
            skFitSpline(sketch, "E293", {"points": [v(32.48, 27.36) * mm, v(33, 27.78) * mm, v(33.05, 27.91) * mm, v(32.96, 28.95) * mm]});
            skFitSpline(sketch, "E294", {"points": [v(32.96, 28.95) * mm, v(32.91, 29.57) * mm, v(32.82, 30.13) * mm, v(32.76, 30.19) * mm]});
            skFitSpline(sketch, "E295", {"points": [v(32.76, 30.19) * mm, v(32.7, 30.25) * mm, v(32.3, 30.15) * mm, v(31.89, 29.97) * mm]});
            skFitSpline(sketch, "E296", {"points": [v(31.89, 29.97) * mm, v(31.46, 29.8) * mm, v(31.06, 29.65) * mm, v(30.98, 29.65) * mm]});
            skFitSpline(sketch, "E297", {"points": [v(30.98, 29.65) * mm, v(30.9, 29.65) * mm, v(30.9, 30.37) * mm, v(30.97, 31.24) * mm]});
            skFitSpline(sketch, "E298", {"points": [v(30.97, 31.24) * mm, v(31.1, 32.73) * mm, v(31.07, 32.83) * mm, v(30.68, 32.83) * mm]});
            skFitSpline(sketch, "E299", {"points": [v(30.68, 32.83) * mm, v(30.45, 32.83) * mm, v(30.26, 32.97) * mm, v(30.26, 33.15) * mm]});
            skFitSpline(sketch, "E300", {"points": [v(30.26, 33.15) * mm, v(30.26, 33.32) * mm, v(30.16, 33.46) * mm, v(30.05, 33.46) * mm]});
            skFitSpline(sketch, "E301", {"points": [v(30.05, 33.46) * mm, v(29.69, 33.46) * mm, v(29.82, 34.44) * mm, v(30.23, 34.81) * mm]});
            skFitSpline(sketch, "E302", {"points": [v(30.23, 34.81) * mm, v(30.44, 35) * mm, v(31.16, 35.28) * mm, v(31.83, 35.42) * mm]});
            skFitSpline(sketch, "E303", {"points": [v(31.83, 35.42) * mm, v(32.85, 35.63) * mm, v(33.13, 35.62) * mm, v(33.6, 35.36) * mm]});
            skFitSpline(sketch, "E304", {"points": [v(33.6, 35.36) * mm, v(34.37, 34.93) * mm, v(34.48, 34.05) * mm, v(33.82, 33.73) * mm]});
            skFitSpline(sketch, "E305", {"points": [v(33.82, 33.73) * mm, v(33.34, 33.51) * mm, v(33.35, 33.5) * mm, v(34.15, 33.16) * mm]});
            skFitSpline(sketch, "E306", {"points": [v(34.15, 33.16) * mm, v(34.9, 32.83) * mm, v(34.99, 32.83) * mm, v(35.36, 33.17) * mm]});
            skFitSpline(sketch, "E307", {"points": [v(35.36, 33.17) * mm, v(35.58, 33.37) * mm, v(35.76, 33.64) * mm, v(35.76, 33.77) * mm]});
            skFitSpline(sketch, "E308", {"points": [v(35.76, 33.77) * mm, v(35.76, 33.9) * mm, v(36.1, 34.7) * mm, v(36.5, 35.56) * mm]});
            skFitSpline(sketch, "E309", {"points": [v(36.5, 35.56) * mm, v(37.29, 37.18) * mm, v(37.3, 37.75) * mm, v(36.61, 38.12) * mm]});
            skFitSpline(sketch, "E310", {"points": [v(36.61, 38.12) * mm, v(36.14, 38.38) * mm, v(35.55, 38.19) * mm, v(35.55, 37.78) * mm]});
            skFitSpline(sketch, "E311", {"points": [v(35.55, 37.78) * mm, v(35.55, 36.66) * mm, v(30.79, 39.12) * mm, v(30.36, 40.45) * mm]});
            skFitSpline(sketch, "E312", {"points": [v(30.36, 40.45) * mm, v(30.3, 40.68) * mm, v(30.34, 41.05) * mm, v(30.47, 41.29) * mm]});
            skFitSpline(sketch, "E313", {"points": [v(30.47, 41.29) * mm, v(30.77, 41.86) * mm, v(31.55, 41.83) * mm, v(33.01, 41.2) * mm]});
            skFitSpline(sketch, "E314", {"points": [v(33.01, 41.2) * mm, v(34.25, 40.67) * mm, v(34.4, 40.66) * mm, v(34.2, 41.18) * mm]});
            skFitSpline(sketch, "E315", {"points": [v(34.2, 41.18) * mm, v(34.13, 41.4) * mm, v(33.81, 41.5) * mm, v(33.34, 41.5) * mm]});
            skFitSpline(sketch, "E316", {"points": [v(33.34, 41.5) * mm, v(32.48, 41.5) * mm, v(32.37, 41.83) * mm, v(32.97, 42.57) * mm]});
            skFitSpline(sketch, "E317", {"points": [v(32.97, 42.57) * mm, v(33.3, 42.96) * mm, v(33.56, 43.04) * mm, v(34.54, 43.04) * mm]});
            skFitSpline(sketch, "E318", {"points": [v(34.54, 43.04) * mm, v(36.05, 43.02) * mm, v(36.12, 43.25) * mm, v(35.4, 45.67) * mm]});
            skFitSpline(sketch, "E319", {"points": [v(35.4, 45.67) * mm, v(34.98, 47.1) * mm, v(34.9, 47.7) * mm, v(35.01, 48.62) * mm]});
            skFitSpline(sketch, "E320", {"points": [v(35.01, 48.62) * mm, v(35.1, 49.37) * mm, v(35.26, 49.76) * mm, v(35.45, 49.76) * mm]});
            skFitSpline(sketch, "E321", {"points": [v(35.45, 49.76) * mm, v(35.79, 49.76) * mm, v(36.46, 48.04) * mm, v(36.81, 46.27) * mm]});
            skFitSpline(sketch, "E322", {"points": [v(36.81, 46.27) * mm, v(37.15, 44.53) * mm, v(37.45, 43.62) * mm, v(37.68, 43.62) * mm]});
            skFitSpline(sketch, "E323", {"points": [v(37.68, 43.62) * mm, v(37.8, 43.62) * mm, v(37.88, 43.84) * mm, v(37.88, 44.1) * mm]});
            skFitSpline(sketch, "E324", {"points": [v(37.88, 44.1) * mm, v(37.88, 44.74) * mm, v(36.88, 48.83) * mm, v(36.6, 49.36) * mm]});
            skFitSpline(sketch, "E325", {"points": [v(36.6, 49.36) * mm, v(36.47, 49.6) * mm, v(36.29, 50.3) * mm, v(36.19, 50.92) * mm]});
            skFitSpline(sketch, "E326", {"points": [v(36.19, 50.92) * mm, v(36.09, 51.54) * mm, v(35.8, 52.48) * mm, v(35.57, 53.01) * mm]});
            skFitSpline(sketch, "E327", {"points": [v(35.57, 53.01) * mm, v(35.31, 53.57) * mm, v(35.13, 54.41) * mm, v(35.13, 55.03) * mm]});
            skFitSpline(sketch, "E328", {"points": [v(35.13, 55.03) * mm, v(35.13, 56.37) * mm, v(34.52, 57.14) * mm, v(33.05, 57.66) * mm]});
            skFitSpline(sketch, "E329", {"points": [v(33.05, 57.66) * mm, v(31.97, 58.05) * mm, v(31.44, 58.5) * mm, v(31.02, 59.34) * mm]});
            skFitSpline(sketch, "E330", {"points": [v(31.02, 59.34) * mm, v(30.64, 60.08) * mm, v(29.4, 60.31) * mm, v(25.6, 60.34) * mm]});
            skFitSpline(sketch, "E331", {"points": [v(25.6, 60.34) * mm, v(21.36, 60.37) * mm, v(20.2, 60.66) * mm, v(19.62, 61.83) * mm]});
            skFitSpline(sketch, "E332", {"points": [v(19.62, 61.83) * mm, v(19.42, 62.24) * mm, v(19.25, 63.05) * mm, v(19.25, 63.63) * mm]});
            skFitSpline(sketch, "E333", {"points": [v(19.25, 63.63) * mm, v(19.24, 64.97) * mm, v(18.71, 66.14) * mm, v(17.39, 67.73) * mm]});
            skFitSpline(sketch, "E334", {"points": [v(17.39, 67.73) * mm, v(15.95, 69.45) * mm, v(15.56, 70.55) * mm, v(15.72, 72.4) * mm]});
            skFitSpline(sketch, "E335", {"points": [v(15.72, 72.4) * mm, v(15.89, 74.42) * mm, v(15.61, 75.26) * mm, v(14.57, 75.97) * mm]});
            skFitSpline(sketch, "E336", {"points": [v(14.57, 75.97) * mm, v(13.8, 76.48) * mm, v(12.94, 77.13) * mm, v(10.52, 78.96) * mm]});
            skFitSpline(sketch, "E337", {"points": [v(10.52, 78.96) * mm, v(9.93, 79.4) * mm, v(9.37, 79.6) * mm, v(8.4, 79.72) * mm]});
            skFitSpline(sketch, "E338", {"points": [v(8.4, 79.72) * mm, v(7.67, 79.8) * mm, v(6.83, 80.05) * mm, v(6.52, 80.27) * mm]});
            skFitSpline(sketch, "E339", {"points": [v(6.52, 80.27) * mm, v(5.73, 80.83) * mm, v(4.99, 80.76) * mm, v(4.18, 80.06) * mm]});
            skFitSpline(sketch, "E340", {"points": [v(4.18, 80.06) * mm, v(3.06, 79.09) * mm, v(2.62, 78.93) * mm, v(1.4, 79.08) * mm]});
            skFitSpline(sketch, "E341", {"points": [v(-1.23, 77.67) * mm, v(-2.35, 76.53) * mm, v(-2.88, 75.8) * mm, v(-3.2, 74.95) * mm]});
            skFitSpline(sketch, "E342", {"points": [v(-3.2, 74.95) * mm, v(-3.44, 74.31) * mm, v(-3.84, 73.58) * mm, v(-4.08, 73.32) * mm]});
            skFitSpline(sketch, "E343", {"points": [v(-4.08, 73.32) * mm, v(-4.6, 72.75) * mm, v(-5.86, 72.28) * mm, v(-7.31, 72.1) * mm]});
            skFitSpline(sketch, "E344", {"points": [v(-7.31, 72.1) * mm, v(-8.5, 71.94) * mm, v(-9.16, 71.58) * mm, v(-9.92, 70.68) * mm]});
            skFitSpline(sketch, "E345", {"points": [v(-9.92, 70.68) * mm, v(-10.62, 69.85) * mm, v(-11.46, 69.45) * mm, v(-12.51, 69.45) * mm]});
            skFitSpline(sketch, "E346", {"points": [v(-13.27, 67.07) * mm, v(-13.12, 64.4) * mm, v(-13.35, 63.34) * mm, v(-14.15, 63) * mm]});
            skFitSpline(sketch, "E347", {"points": [v(-14.15, 63) * mm, v(-14.41, 62.88) * mm, v(-14.68, 62.54) * mm, v(-14.74, 62.25) * mm]});
            skFitSpline(sketch, "E348", {"points": [v(-14.74, 62.25) * mm, v(-14.95, 61.27) * mm, v(-15.22, 60.8) * mm, v(-15.67, 60.66) * mm]});
            skFitSpline(sketch, "E349", {"points": [v(-15.67, 60.66) * mm, v(-16.3, 60.47) * mm, v(-17.15, 61.07) * mm, v(-17.15, 61.71) * mm]});
            skFitSpline(sketch, "E350", {"points": [v(-17.15, 61.71) * mm, v(-17.15, 62.4) * mm, v(-17.57, 62.62) * mm, v(-17.95, 62.12) * mm]});
            skFitSpline(sketch, "E351", {"points": [v(-17.95, 62.12) * mm, v(-18.25, 61.72) * mm, v(-18.24, 60.86) * mm, v(-17.87, 57.55) * mm]});
            skFitSpline(sketch, "E352", {"points": [v(-17.87, 57.55) * mm, v(-17.76, 56.53) * mm, v(-17.83, 56.11) * mm, v(-18.31, 54.9) * mm]});
            skFitSpline(sketch, "E353", {"points": [v(-18.43, 53.1) * mm, v(-18.09, 52.84) * mm, v(-18, 52.61) * mm, v(-18.12, 52.26) * mm]});
            skFitSpline(sketch, "E354", {"points": [v(-18.12, 52.26) * mm, v(-18.35, 51.5) * mm, v(-18.6, 51.29) * mm, v(-19.44, 51.14) * mm]});
            skFitSpline(sketch, "E355", {"points": [v(-19.44, 51.14) * mm, v(-20.16, 51.02) * mm, v(-20.25, 50.92) * mm, v(-20.59, 49.92) * mm]});
            skFitSpline(sketch, "E356", {"points": [v(-20.59, 49.92) * mm, v(-21.07, 48.49) * mm, v(-20.79, 47.82) * mm, v(-19.64, 47.63) * mm]});
            skFitSpline(sketch, "E357", {"points": [v(-19.64, 47.63) * mm, v(-18.7, 47.48) * mm, v(-18.1, 46.98) * mm, v(-17.9, 46.22) * mm]});
            skFitSpline(sketch, "E358", {"points": [v(-17.9, 46.22) * mm, v(-17.82, 45.92) * mm, v(-17.92, 44.77) * mm, v(-18.12, 43.68) * mm]});
            skFitSpline(sketch, "E359", {"points": [v(-18.12, 43.68) * mm, v(-18.44, 41.9) * mm, v(-18.54, 41.66) * mm, v(-19.03, 41.44) * mm]});
            skFitSpline(sketch, "E360", {"points": [v(-19.03, 41.44) * mm, v(-19.33, 41.3) * mm, v(-19.75, 41.02) * mm, v(-19.96, 40.82) * mm]});
            skFitSpline(sketch, "E361", {"points": [v(-19.96, 40.82) * mm, v(-20.16, 40.62) * mm, v(-20.6, 40.45) * mm, v(-20.94, 40.45) * mm]});
            skFitSpline(sketch, "E362", {"points": [v(-21.44, 41.8) * mm, v(-21.32, 43.27) * mm, v(-21.6, 44.43) * mm, v(-22.21, 44.98) * mm]});
            skFitSpline(sketch, "E363", {"points": [v(-22.21, 44.98) * mm, v(-22.54, 45.28) * mm, v(-22.7, 45.3) * mm, v(-23.16, 45.08) * mm]});
            skFitSpline(sketch, "E364", {"points": [v(-23.16, 45.08) * mm, v(-23.48, 44.93) * mm, v(-23.72, 44.65) * mm, v(-23.72, 44.41) * mm]});
            skFitSpline(sketch, "E365", {"points": [v(-23.72, 44.41) * mm, v(-23.72, 44.19) * mm, v(-24.06, 43.69) * mm, v(-24.47, 43.3) * mm]});
            skFitSpline(sketch, "E366", {"points": [v(-24.8, 41.05) * mm, v(-24.28, 39.2) * mm, v(-24.4, 38.43) * mm, v(-25.38, 37) * mm]});
            skFitSpline(sketch, "E367", {"points": [v(-25.38, 37) * mm, v(-26.38, 35.55) * mm, v(-26.52, 35.03) * mm, v(-26.15, 34.3) * mm]});
            skFitSpline(sketch, "E368", {"points": [v(-26.15, 34.3) * mm, v(-25.74, 33.52) * mm, v(-25.75, 32.64) * mm, v(-26.17, 31.34) * mm]});
            skFitSpline(sketch, "E369", {"points": [v(-26.17, 31.34) * mm, v(-26.5, 30.34) * mm, v(-26.5, 30.27) * mm, v(-26.05, 29.35) * mm]});
            skFitSpline(sketch, "E370", {"points": [v(-26.05, 29.35) * mm, v(-25.45, 28.12) * mm, v(-24.64, 27.64) * mm, v(-22.5, 27.27) * mm]});
            skFitSpline(sketch, "E371", {"points": [v(-22.5, 27.27) * mm, v(-21.03, 27.01) * mm, v(-20.71, 27.01) * mm, v(-20.51, 27.25) * mm]});
            skFitSpline(sketch, "E372", {"points": [v(-20.51, 27.25) * mm, v(-20.2, 27.62) * mm, v(-19.6, 27.62) * mm, v(-19.29, 27.24) * mm]});
            skFitSpline(sketch, "E373", {"points": [v(-19.29, 27.24) * mm, v(-18.74, 26.58) * mm, v(-18.77, 25.45) * mm, v(-19.37, 23.93) * mm]});
            skFitSpline(sketch, "E374", {"points": [v(-19.37, 23.93) * mm, v(-19.7, 23.08) * mm, v(-20.07, 22.46) * mm, v(-20.24, 22.46) * mm]});
            skFitSpline(sketch, "E375", {"points": [v(-20.24, 22.46) * mm, v(-20.4, 22.46) * mm, v(-20.54, 22.54) * mm, v(-20.54, 22.65) * mm]});
            skFitSpline(sketch, "E376", {"points": [v(-20.54, 22.65) * mm, v(-20.54, 23.08) * mm, v(-22.27, 25) * mm, v(-22.65, 25) * mm]});
            skFitSpline(sketch, "E377", {"points": [v(-22.65, 25) * mm, v(-23.23, 25) * mm, v(-23.72, 24.2) * mm, v(-23.72, 23.22) * mm]});
            skFitSpline(sketch, "E378", {"points": [v(-23.72, 23.22) * mm, v(-23.72, 22.72) * mm, v(-23.92, 22.04) * mm, v(-24.24, 21.5) * mm]});
            skFitSpline(sketch, "E379", {"points": [v(-24.24, 21.5) * mm, v(-24.66, 20.79) * mm, v(-24.75, 20.34) * mm, v(-24.74, 19.26) * mm]});
            skFitSpline(sketch, "E380", {"points": [v(-24.74, 19.26) * mm, v(-24.72, 18.51) * mm, v(-24.78, 17.69) * mm, v(-24.86, 17.43) * mm]});
            skFitSpline(sketch, "E381", {"points": [v(-24.86, 17.43) * mm, v(-25.08, 16.75) * mm, v(-24.82, 16.1) * mm, v(-24.33, 16.1) * mm]});
            skFitSpline(sketch, "E382", {"points": [v(-24.33, 16.1) * mm, v(-23.36, 16.1) * mm, v(-23.83, 14.55) * mm, v(-24.88, 14.3) * mm]});
            skFitSpline(sketch, "E383", {"points": [v(-24.88, 14.3) * mm, v(-25.3, 14.18) * mm, v(-25.36, 14.09) * mm, v(-25.2, 13.77) * mm]});
            skFitSpline(sketch, "E384", {"points": [v(-25.2, 13.77) * mm, v(-24.96, 13.34) * mm, v(-24.91, 12.23) * mm, v(-25.11, 12.03) * mm]});
            skFitSpline(sketch, "E385", {"points": [v(-25.11, 12.03) * mm, v(-25.18, 11.96) * mm, v(-25.46, 11.98) * mm, v(-25.73, 12.09) * mm]});
            skFitSpline(sketch, "E386", {"points": [v(-25.73, 12.09) * mm, v(-26.03, 12.2) * mm, v(-26.5, 12.18) * mm, v(-26.98, 12.04) * mm]});
            skFitSpline(sketch, "E387", {"points": [v(-26.98, 12.04) * mm, v(-28.78, 11.48) * mm, v(-28.79, 13.48) * mm, v(-26.99, 14.98) * mm]});
            skFitSpline(sketch, "E388", {"points": [v(-26.99, 14.98) * mm, v(-26.47, 15.42) * mm, v(-26.04, 15.92) * mm, v(-26.04, 16.09) * mm]});
            skFitSpline(sketch, "E389", {"points": [v(-26.04, 16.09) * mm, v(-26.04, 16.33) * mm, v(-26.1, 16.35) * mm, v(-26.3, 16.15) * mm]});
            skFitSpline(sketch, "E390", {"points": [v(-26.3, 16.15) * mm, v(-26.76, 15.69) * mm, v(-27.73, 15.86) * mm, v(-28.39, 16.52) * mm]});
            skFitSpline(sketch, "E391", {"points": [v(-28.39, 16.52) * mm, v(-28.98, 17.1) * mm, v(-29, 17.22) * mm, v(-29, 18.97) * mm]});
            skFitSpline(sketch, "E392", {"points": [v(-29, 18.97) * mm, v(-29, 20.63) * mm, v(-29.05, 20.82) * mm, v(-29.43, 20.91) * mm]});
            skFitSpline(sketch, "E393", {"points": [v(-29.43, 20.91) * mm, v(-30.19, 21.11) * mm, v(-29.94, 22.23) * mm, v(-28.69, 24.26) * mm]});
            skFitSpline(sketch, "E394", {"points": [v(-28.69, 24.26) * mm, v(-27.87, 25.58) * mm, v(-28, 27.33) * mm, v(-28.9, 27.33) * mm]});
            skFitSpline(sketch, "E395", {"points": [v(-28.9, 27.33) * mm, v(-29.17, 27.33) * mm, v(-29.7, 27.61) * mm, v(-30.07, 27.96) * mm]});
            skFitSpline(sketch, "E396", {"points": [v(-30.07, 27.96) * mm, v(-30.87, 28.71) * mm, v(-31.12, 28.76) * mm, v(-31.12, 28.14) * mm]});
            skFitSpline(sketch, "E397", {"points": [v(-31.12, 28.14) * mm, v(-31.12, 27.9) * mm, v(-30.7, 27.23) * mm, v(-30.17, 26.67) * mm]});
            skFitSpline(sketch, "E398", {"points": [v(-30.17, 26.67) * mm, v(-29.12, 25.55) * mm, v(-29.07, 25.4) * mm, v(-29.55, 24.9) * mm]});
            skFitSpline(sketch, "E399", {"points": [v(-29.55, 24.9) * mm, v(-30.1, 24.36) * mm, v(-30.96, 24.5) * mm, v(-31.6, 25.23) * mm]});
            skFitSpline(sketch, "E400", {"points": [v(-31.6, 25.23) * mm, v(-32.15, 25.85) * mm, v(-32.25, 25.88) * mm, v(-33.19, 25.74) * mm]});
            skFitSpline(sketch, "E401", {"points": [v(-33.19, 25.74) * mm, v(-34.37, 25.57) * mm, v(-35.26, 25.15) * mm, v(-35.43, 24.68) * mm]});
            skFitSpline(sketch, "E402", {"points": [v(-35.43, 24.68) * mm, v(-35.6, 24.23) * mm, v(-35.14, 24.08) * mm, v(-34.43, 24.35) * mm]});
            skFitSpline(sketch, "E403", {"points": [v(-34.43, 24.35) * mm, v(-34.1, 24.48) * mm, v(-33.54, 24.57) * mm, v(-33.15, 24.57) * mm]});
            skFitSpline(sketch, "E404", {"points": [v(-33.15, 24.57) * mm, v(-32.54, 24.57) * mm, v(-32.46, 24.5) * mm, v(-32.44, 24) * mm]});
            skFitSpline(sketch, "E405", {"points": [v(-32.44, 24) * mm, v(-32.43, 23.67) * mm, v(-32.27, 23.06) * mm, v(-32.1, 22.62) * mm]});
            skFitSpline(sketch, "E406", {"points": [v(-32.1, 22.62) * mm, v(-31.58, 21.42) * mm, v(-31.67, 20.28) * mm, v(-32.4, 18.86) * mm]});
            skFitSpline(sketch, "E407", {"points": [v(-32.4, 18.86) * mm, v(-33.14, 17.4) * mm, v(-33.17, 17.05) * mm, v(-32.63, 16.75) * mm]});
            skFitSpline(sketch, "E408", {"points": [v(-32.63, 16.75) * mm, v(-32.1, 16.47) * mm, v(-31.55, 14.82) * mm, v(-31.55, 13.54) * mm]});
            skFitSpline(sketch, "E409", {"points": [v(-31.55, 13.54) * mm, v(-31.55, 12.77) * mm, v(-31.45, 12.46) * mm, v(-31.11, 12.23) * mm]});
            skFitSpline(sketch, "E410", {"points": [v(-31.11, 12.23) * mm, v(-30.88, 12.06) * mm, v(-30.63, 11.6) * mm, v(-30.56, 11.18) * mm]});
            skFitSpline(sketch, "E411", {"points": [v(-30.56, 11.18) * mm, v(-30.46, 10.56) * mm, v(-30.52, 10.4) * mm, v(-30.91, 10.18) * mm]});
            skFitSpline(sketch, "E412", {"points": [v(-30.91, 10.18) * mm, v(-31.53, 9.85) * mm, v(-32.75, 10.1) * mm, v(-33.03, 10.6) * mm]});
            skFitSpline(sketch, "E413", {"points": [v(-33.03, 10.6) * mm, v(-33.14, 10.82) * mm, v(-33.25, 11.41) * mm, v(-33.26, 11.91) * mm]});
            skFitSpline(sketch, "E414", {"points": [v(-33.26, 11.91) * mm, v(-33.27, 12.53) * mm, v(-33.55, 13.4) * mm, v(-34.16, 14.63) * mm]});
            skFitSpline(sketch, "E415", {"points": [v(-34.16, 14.63) * mm, v(-34.97, 16.28) * mm, v(-35.1, 16.43) * mm, v(-35.72, 16.5) * mm]});
            skFitSpline(sketch, "E416", {"points": [v(-35.72, 16.5) * mm, v(-36.31, 16.55) * mm, v(-36.58, 16.38) * mm, v(-37.73, 15.23) * mm]});
            skFitSpline(sketch, "E417", {"points": [v(-37.73, 15.23) * mm, v(-38.93, 14.04) * mm, v(-39.01, 13.9) * mm, v(-38.59, 13.83) * mm]});
            skFitSpline(sketch, "E418", {"points": [v(-38.59, 13.83) * mm, v(-38.17, 13.76) * mm, v(-38.1, 13.62) * mm, v(-38.11, 12.76) * mm]});
            skFitSpline(sketch, "E419", {"points": [v(-38.11, 12.76) * mm, v(-38.12, 12.21) * mm, v(-38.4, 10.97) * mm, v(-38.75, 9.98) * mm]});
            skFitSpline(sketch, "E420", {"points": [v(-38.75, 9.98) * mm, v(-39.51, 7.8) * mm, v(-39.52, 7.37) * mm, v(-38.83, 5.2) * mm]});
            skFitSpline(sketch, "E421", {"points": [v(-38.83, 5.2) * mm, v(-38.38, 3.8) * mm, v(-38.3, 3.15) * mm, v(-38.32, 1.4) * mm]});
            skFitSpline(sketch, "E422", {"points": [v(-38.32, 1.4) * mm, v(-38.34, 0.23) * mm, v(-38.26, -1.1) * mm, v(-38.13, -1.57) * mm]});
            skFitSpline(sketch, "E423", {"points": [v(-38.13, -1.57) * mm, v(-37.77, -2.92) * mm, v(-37.86, -6.07) * mm, v(-38.34, -8.88) * mm]});
            skFitSpline(sketch, "E424", {"points": [v(-38.34, -8.88) * mm, v(-38.63, -10.58) * mm, v(-38.76, -12.12) * mm, v(-38.71, -13.3) * mm]});
            skFitSpline(sketch, "E425", {"points": [v(-38.71, -13.3) * mm, v(-38.65, -14.92) * mm, v(-38.56, -15.24) * mm, v(-37.96, -16.18) * mm]});
            skFitSpline(sketch, "E426", {"points": [v(-37.41, -20.41) * mm, v(-37.55, -24.06) * mm, v(-37.43, -24.65) * mm, v(-36.22, -26.18) * mm]});
            skFitSpline(sketch, "E427", {"points": [v(-36.22, -26.18) * mm, v(-34.5, -28.36) * mm, v(-33.66, -30.2) * mm, v(-33.66, -31.8) * mm]});
            skFitSpline(sketch, "E428", {"points": [v(-33.66, -31.8) * mm, v(-33.66, -32.5) * mm, v(-33.82, -32.8) * mm, v(-34.62, -33.66) * mm]});
            skFitSpline(sketch, "E429", {"points": [v(-34.62, -33.66) * mm, v(-35.46, -34.56) * mm, v(-35.57, -34.79) * mm, v(-35.57, -35.64) * mm]});
            skFitSpline(sketch, "E430", {"points": [v(-35.57, -35.64) * mm, v(-35.57, -36.85) * mm, v(-35.16, -37.86) * mm, v(-34.2, -38.96) * mm]});
            skFitSpline(sketch, "E431", {"points": [v(-34.2, -38.96) * mm, v(-33.8, -39.44) * mm, v(-33.28, -40.4) * mm, v(-33.04, -41.1) * mm]});
            skFitSpline(sketch, "E432", {"points": [v(-33.04, -41.1) * mm, v(-32.76, -41.93) * mm, v(-32.24, -42.8) * mm, v(-31.56, -43.59) * mm]});
            skFitSpline(sketch, "E433", {"points": [v(-31.56, -43.59) * mm, v(-29.64, -45.8) * mm, v(-29.61, -45.88) * mm, v(-29.6, -49.55) * mm]});
            skFitSpline(sketch, "E434", {"points": [v(-29.6, -49.55) * mm, v(-29.59, -51.33) * mm, v(-29.65, -53.1) * mm, v(-29.74, -53.47) * mm]});
            skFitSpline(sketch, "E435", {"points": [v(-29.74, -53.47) * mm, v(-29.87, -54.05) * mm, v(-29.78, -54.34) * mm, v(-29.2, -55.24) * mm]});
            skFitSpline(sketch, "E436", {"points": [v(-29.2, -55.24) * mm, v(-28.02, -57.1) * mm, v(-28.34, -58.63) * mm, v(-30.4, -60.92) * mm]});
            skFitSpline(sketch, "E437", {"points": [v(-30.9, -63.02) * mm, v(-30.62, -63.56) * mm, v(-29.54, -65.09) * mm, v(-28.5, -66.4) * mm]});
            skFitSpline(sketch, "E438", {"points": [v(-28.5, -66.4) * mm, v(-27.47, -67.73) * mm, v(-25.87, -70.02) * mm, v(-24.93, -71.5) * mm]});
            skFitSpline(sketch, "E439", {"points": [v(-24.93, -71.5) * mm, v(-21.66, -76.64) * mm, v(-20.53, -77.82) * mm, v(-18.3, -78.38) * mm]});
            skFitSpline(sketch, "E440", {"points": [v(-18.3, -78.38) * mm, v(-17.5, -78.58) * mm, v(-15.88, -79.13) * mm, v(-14.72, -79.6) * mm]});
            skFitSpline(sketch, "E441", {"points": [v(-14.72, -79.6) * mm, v(-13.56, -80.07) * mm, v(-12.22, -80.53) * mm, v(-11.76, -80.63) * mm]});
            skFitSpline(sketch, "E442", {"points": [v(-11.76, -80.63) * mm, v(-10.67, -80.86) * mm, v(-8.14, -80.7) * mm, v(-6.84, -80.3) * mm]});
            skFitSpline(sketch, "E443", {"points": [v(-34.5, 19.17) * mm, v(-34.65, 19.34) * mm, v(-35.11, 19.55) * mm, v(-35.54, 19.62) * mm]});
            skFitSpline(sketch, "E444", {"points": [v(-35.54, 19.62) * mm, v(-35.99, 19.7) * mm, v(-36.79, 20.15) * mm, v(-37.44, 20.68) * mm]});
            skFitSpline(sketch, "E445", {"points": [v(-37.44, 20.68) * mm, v(-38.07, 21.2) * mm, v(-38.96, 21.72) * mm, v(-39.42, 21.86) * mm]});
            skFitSpline(sketch, "E446", {"points": [v(-39.42, 21.86) * mm, v(-39.89, 22) * mm, v(-40.41, 22.34) * mm, v(-40.6, 22.6) * mm]});
            skFitSpline(sketch, "E447", {"points": [v(-40.6, 22.6) * mm, v(-40.88, 23.06) * mm, v(-40.88, 23.2) * mm, v(-40.52, 24.1) * mm]});
            skFitSpline(sketch, "E448", {"points": [v(-40.52, 24.1) * mm, v(-39.98, 25.46) * mm, v(-39.97, 28.27) * mm, v(-40.5, 29.07) * mm]});
            skFitSpline(sketch, "E449", {"points": [v(-40.5, 29.07) * mm, v(-40.94, 29.76) * mm, v(-40.96, 30.33) * mm, v(-40.55, 31.12) * mm]});
            skFitSpline(sketch, "E450", {"points": [v(-40.55, 31.12) * mm, v(-40.35, 31.5) * mm, v(-40.29, 32) * mm, v(-40.37, 32.52) * mm]});
            skFitSpline(sketch, "E451", {"points": [v(-40.37, 32.52) * mm, v(-40.49, 33.2) * mm, v(-40.43, 33.39) * mm, v(-39.97, 33.76) * mm]});
            skFitSpline(sketch, "E452", {"points": [v(-39.97, 33.76) * mm, v(-39.45, 34.2) * mm, v(-38.12, 36.16) * mm, v(-37.84, 36.9) * mm]});
            skFitSpline(sketch, "E453", {"points": [v(-37.84, 36.9) * mm, v(-37.74, 37.17) * mm, v(-37.47, 37.27) * mm, v(-36.87, 37.27) * mm]});
            skFitSpline(sketch, "E454", {"points": [v(-36.87, 37.27) * mm, v(-36.4, 37.27) * mm, v(-35.93, 37.4) * mm, v(-35.78, 37.6) * mm]});
            skFitSpline(sketch, "E455", {"points": [v(-35.78, 37.6) * mm, v(-35.64, 37.77) * mm, v(-35.2, 37.9) * mm, v(-34.82, 37.9) * mm]});
            skFitSpline(sketch, "E456", {"points": [v(-34.82, 37.9) * mm, v(-34.13, 37.9) * mm, v(-34.12, 37.9) * mm, v(-34.23, 37.12) * mm]});
            skFitSpline(sketch, "E457", {"points": [v(-34.23, 37.12) * mm, v(-34.47, 35.46) * mm, v(-34.75, 34.75) * mm, v(-35.37, 34.23) * mm]});
            skFitSpline(sketch, "E458", {"points": [v(-35.37, 34.23) * mm, v(-35.99, 33.7) * mm, v(-36, 33.67) * mm, v(-35.67, 33.16) * mm]});
            skFitSpline(sketch, "E459", {"points": [v(-35.67, 33.16) * mm, v(-34.87, 31.95) * mm, v(-36.1, 31.14) * mm, v(-37.5, 31.95) * mm]});
            skFitSpline(sketch, "E460", {"points": [v(-37.5, 31.95) * mm, v(-37.94, 32.2) * mm, v(-38.35, 32.4) * mm, v(-38.4, 32.4) * mm]});
            skFitSpline(sketch, "E461", {"points": [v(-38.4, 32.4) * mm, v(-38.63, 32.4) * mm, v(-38.23, 31.65) * mm, v(-37.44, 30.52) * mm]});
            skFitSpline(sketch, "E462", {"points": [v(-37.44, 30.52) * mm, v(-36.44, 29.1) * mm, v(-36.35, 28.09) * mm, v(-37.16, 27.33) * mm]});
            skFitSpline(sketch, "E463", {"points": [v(-37.16, 27.33) * mm, v(-37.75, 26.77) * mm, v(-37.88, 25.84) * mm, v(-37.36, 25.84) * mm]});
            skFitSpline(sketch, "E464", {"points": [v(-37.36, 25.84) * mm, v(-37.12, 25.84) * mm, v(-37.08, 25.7) * mm, v(-37.18, 25.26) * mm]});
            skFitSpline(sketch, "E465", {"points": [v(-37.18, 25.26) * mm, v(-37.37, 24.47) * mm, v(-37.66, 23.94) * mm, v(-37.9, 23.94) * mm]});
            skFitSpline(sketch, "E466", {"points": [v(-37.9, 23.94) * mm, v(-38.25, 23.94) * mm, v(-38.13, 23.18) * mm, v(-37.73, 22.82) * mm]});
            skFitSpline(sketch, "E467", {"points": [v(-37.73, 22.82) * mm, v(-37.52, 22.63) * mm, v(-36.88, 22.27) * mm, v(-36.3, 22.02) * mm]});
            skFitSpline(sketch, "E468", {"points": [v(-36.3, 22.02) * mm, v(-33.61, 20.87) * mm, v(-33.45, 20.76) * mm, v(-33.45, 20.13) * mm]});
            skFitSpline(sketch, "E469", {"points": [v(-33.45, 20.13) * mm, v(-33.45, 18.94) * mm, v(-33.94, 18.5) * mm, v(-34.5, 19.17) * mm]});
            skFitSpline(sketch, "E470", {"points": [v(-33.88, 20.11) * mm, v(-33.88, 20.2) * mm, v(-34.7, 20.65) * mm, v(-35.7, 21.1) * mm]});
            skFitSpline(sketch, "E471", {"points": [v(-35.7, 21.1) * mm, v(-38.2, 22.21) * mm, v(-38.53, 22.5) * mm, v(-38.53, 23.53) * mm]});
            skFitSpline(sketch, "E472", {"points": [v(-38.53, 23.53) * mm, v(-38.53, 23.99) * mm, v(-38.45, 24.36) * mm, v(-38.35, 24.36) * mm]});
            skFitSpline(sketch, "E473", {"points": [v(-38.35, 24.36) * mm, v(-38.26, 24.36) * mm, v(-38.08, 24.58) * mm, v(-37.96, 24.84) * mm]});
            skFitSpline(sketch, "E474", {"points": [v(-37.96, 24.84) * mm, v(-37.8, 25.2) * mm, v(-37.81, 25.39) * mm, v(-38.03, 25.6) * mm]});
            skFitSpline(sketch, "E475", {"points": [v(-38.03, 25.6) * mm, v(-38.5, 26.03) * mm, v(-38.36, 26.84) * mm, v(-37.67, 27.63) * mm]});
            skFitSpline(sketch, "E476", {"points": [v(-37.67, 27.63) * mm, v(-36.9, 28.51) * mm, v(-36.94, 28.8) * mm, v(-38.14, 30.48) * mm]});
            skFitSpline(sketch, "E477", {"points": [v(-38.14, 30.48) * mm, v(-38.63, 31.17) * mm, v(-38.96, 31.87) * mm, v(-38.96, 32.23) * mm]});
            skFitSpline(sketch, "E478", {"points": [v(-38.96, 32.23) * mm, v(-38.96, 32.75) * mm, v(-38.87, 32.83) * mm, v(-38.36, 32.83) * mm]});
            skFitSpline(sketch, "E479", {"points": [v(-38.36, 32.83) * mm, v(-38.03, 32.83) * mm, v(-37.58, 32.69) * mm, v(-37.36, 32.52) * mm]});
            skFitSpline(sketch, "E480", {"points": [v(-37.36, 32.52) * mm, v(-36.98, 32.23) * mm, v(-36, 32.07) * mm, v(-36, 32.3) * mm]});
            skFitSpline(sketch, "E481", {"points": [v(-36, 32.3) * mm, v(-36, 32.35) * mm, v(-36.15, 32.73) * mm, v(-36.35, 33.14) * mm]});
            skFitSpline(sketch, "E482", {"points": [v(-35.92, 34.57) * mm, v(-35.27, 35.14) * mm, v(-35.1, 35.46) * mm, v(-34.96, 36.38) * mm]});
            skFitSpline(sketch, "E483", {"points": [v(-34.96, 36.38) * mm, v(-34.86, 36.99) * mm, v(-34.82, 37.49) * mm, v(-34.87, 37.49) * mm]});
            skFitSpline(sketch, "E484", {"points": [v(-34.87, 37.49) * mm, v(-34.91, 37.49) * mm, v(-35.23, 37.28) * mm, v(-35.56, 37.04) * mm]});
            skFitSpline(sketch, "E485", {"points": [v(-35.56, 37.04) * mm, v(-35.96, 36.74) * mm, v(-36.36, 36.62) * mm, v(-36.72, 36.69) * mm]});
            skFitSpline(sketch, "E486", {"points": [v(-36.72, 36.69) * mm, v(-37.02, 36.75) * mm, v(-37.26, 36.72) * mm, v(-37.26, 36.64) * mm]});
            skFitSpline(sketch, "E487", {"points": [v(-37.26, 36.64) * mm, v(-37.26, 36.35) * mm, v(-39.4, 33.25) * mm, v(-39.6, 33.25) * mm]});
            skFitSpline(sketch, "E488", {"points": [v(-39.6, 33.25) * mm, v(-39.71, 33.25) * mm, v(-39.8, 32.75) * mm, v(-39.8, 32.14) * mm]});
            skFitSpline(sketch, "E489", {"points": [v(-39.8, 32.14) * mm, v(-39.81, 31.5) * mm, v(-39.95, 30.86) * mm, v(-40.13, 30.62) * mm]});
            skFitSpline(sketch, "E490", {"points": [v(-40.13, 30.62) * mm, v(-40.4, 30.26) * mm, v(-40.4, 30.15) * mm, v(-40.08, 29.67) * mm]});
            skFitSpline(sketch, "E491", {"points": [v(-40.08, 29.67) * mm, v(-39.54, 28.86) * mm, v(-39.43, 25.58) * mm, v(-39.9, 24.18) * mm]});
            skFitSpline(sketch, "E492", {"points": [v(-39.9, 24.18) * mm, v(-40.1, 23.59) * mm, v(-40.2, 23.02) * mm, v(-40.14, 22.92) * mm]});
            skFitSpline(sketch, "E493", {"points": [v(-40.14, 22.92) * mm, v(-40.08, 22.82) * mm, v(-39.57, 22.56) * mm, v(-39.02, 22.35) * mm]});
            skFitSpline(sketch, "E494", {"points": [v(-39.02, 22.35) * mm, v(-38.46, 22.15) * mm, v(-37.5, 21.56) * mm, v(-36.87, 21.05) * mm]});
            skFitSpline(sketch, "E495", {"points": [v(-36.87, 21.05) * mm, v(-36.12, 20.45) * mm, v(-35.53, 20.13) * mm, v(-35.13, 20.13) * mm]});
            skFitSpline(sketch, "E496", {"points": [v(-35.13, 20.13) * mm, v(-34.8, 20.13) * mm, v(-34.48, 20.03) * mm, v(-34.4, 19.91) * mm]});
            skFitSpline(sketch, "E497", {"points": [v(-34.4, 19.91) * mm, v(-34.26, 19.68) * mm, v(-33.88, 19.83) * mm, v(-33.88, 20.11) * mm]});
            skFitSpline(sketch, "E498", {"points": [v(-35.84, 27.25) * mm, v(-35.9, 27.35) * mm, v(-36.01, 27.96) * mm, v(-36.1, 28.6) * mm]});
            skFitSpline(sketch, "E499", {"points": [v(-36.1, 28.6) * mm, v(-36.27, 30.1) * mm, v(-35.9, 30.72) * mm, v(-35.07, 30.34) * mm]});
            skFitSpline(sketch, "E500", {"points": [v(-35.07, 30.34) * mm, v(-34.7, 30.18) * mm, v(-34.56, 29.98) * mm, v(-34.64, 29.77) * mm]});
            skFitSpline(sketch, "E501", {"points": [v(-34.64, 29.77) * mm, v(-34.74, 29.52) * mm, v(-34.61, 29.44) * mm, v(-34.1, 29.44) * mm]});
            skFitSpline(sketch, "E502", {"points": [v(-34.1, 29.44) * mm, v(-33.14, 29.44) * mm, v(-32.6, 29.1) * mm, v(-32.6, 28.48) * mm]});
            skFitSpline(sketch, "E503", {"points": [v(-32.6, 28.48) * mm, v(-32.6, 28.2) * mm, v(-32.71, 27.96) * mm, v(-32.85, 27.96) * mm]});
            skFitSpline(sketch, "E504", {"points": [v(-32.85, 27.96) * mm, v(-32.98, 27.96) * mm, v(-33.2, 27.8) * mm, v(-33.34, 27.62) * mm]});
            skFitSpline(sketch, "E505", {"points": [v(-33.34, 27.62) * mm, v(-33.62, 27.24) * mm, v(-35.65, 26.94) * mm, v(-35.84, 27.25) * mm]});
            skFitSpline(sketch, "E506", {"points": [v(-33.88, 28.07) * mm, v(-33.88, 28.24) * mm, v(-33.73, 28.38) * mm, v(-33.56, 28.38) * mm]});
            skFitSpline(sketch, "E507", {"points": [v(-33.56, 28.38) * mm, v(-33.38, 28.38) * mm, v(-33.24, 28.48) * mm, v(-33.24, 28.6) * mm]});
            skFitSpline(sketch, "E508", {"points": [v(-33.24, 28.6) * mm, v(-33.24, 28.71) * mm, v(-33.73, 28.8) * mm, v(-34.32, 28.8) * mm]});
            skFitSpline(sketch, "E509", {"points": [v(-34.32, 28.8) * mm, v(-35.4, 28.8) * mm, v(-35.4, 28.81) * mm, v(-35.31, 29.43) * mm]});
            skFitSpline(sketch, "E510", {"points": [v(-35.31, 29.43) * mm, v(-35.26, 29.77) * mm, v(-35.3, 30) * mm, v(-35.4, 29.95) * mm]});
            skFitSpline(sketch, "E511", {"points": [v(-35.4, 29.95) * mm, v(-35.6, 29.82) * mm, v(-35.62, 28.91) * mm, v(-35.44, 28.23) * mm]});
            skFitSpline(sketch, "E512", {"points": [v(-35.44, 28.23) * mm, v(-35.33, 27.85) * mm, v(-35.16, 27.75) * mm, v(-34.6, 27.75) * mm]});
            skFitSpline(sketch, "E513", {"points": [v(-34.6, 27.75) * mm, v(-34.1, 27.75) * mm, v(-33.88, 27.85) * mm, v(-33.88, 28.07) * mm]});
            skFitSpline(sketch, "E514", {"points": [v(-34.5, 30.49) * mm, v(-34.87, 31.18) * mm, v(-34.75, 31.97) * mm, v(-34.2, 32.53) * mm]});
            skFitSpline(sketch, "E515", {"points": [v(-34.2, 32.53) * mm, v(-33.9, 32.82) * mm, v(-33.66, 33.2) * mm, v(-33.66, 33.37) * mm]});
            skFitSpline(sketch, "E516", {"points": [v(-33.66, 33.37) * mm, v(-33.66, 33.54) * mm, v(-33.57, 33.68) * mm, v(-33.45, 33.68) * mm]});
            skFitSpline(sketch, "E517", {"points": [v(-33.45, 33.68) * mm, v(-33.34, 33.68) * mm, v(-33.24, 33.6) * mm, v(-33.24, 33.51) * mm]});
            skFitSpline(sketch, "E518", {"points": [v(-33.24, 33.51) * mm, v(-33.24, 33.42) * mm, v(-32.95, 33.24) * mm, v(-32.6, 33.1) * mm]});
            skFitSpline(sketch, "E519", {"points": [v(-32.6, 33.1) * mm, v(-31.72, 32.77) * mm, v(-31.8, 32.27) * mm, v(-32.94, 31.08) * mm]});
            skFitSpline(sketch, "E520", {"points": [v(-32.94, 31.08) * mm, v(-34, 29.96) * mm, v(-34.19, 29.9) * mm, v(-34.5, 30.49) * mm]});
            skFitSpline(sketch, "E521", {"points": [v(-32.6, 32.45) * mm, v(-32.6, 32.54) * mm, v(-32.75, 32.62) * mm, v(-32.92, 32.62) * mm]});
            skFitSpline(sketch, "E522", {"points": [v(-32.92, 32.62) * mm, v(-33.1, 32.62) * mm, v(-33.24, 32.53) * mm, v(-33.24, 32.43) * mm]});
            skFitSpline(sketch, "E523", {"points": [v(-33.24, 32.43) * mm, v(-33.24, 32.33) * mm, v(-33.43, 32.2) * mm, v(-33.66, 32.13) * mm]});
            skFitSpline(sketch, "E524", {"points": [v(-33.66, 32.13) * mm, v(-33.96, 32.06) * mm, v(-34.09, 31.84) * mm, v(-34.09, 31.43) * mm]});
            skFitSpline(sketch, "E525", {"points": [v(-33.35, 31.56) * mm, v(-32.94, 31.95) * mm, v(-32.6, 32.35) * mm, v(-32.6, 32.45) * mm]});
            skSolve(sketch);
        }
        {
            var Q0;
            Q0=makeQuery(id+"F0.imprint","IMPRINT",FACE,{"disambiguationData":[TD([[makeQuery(id+"F0.imprint","IMPRINT",EDGE,{"derivedFrom":sQuery(id+"F0.wireOp",EDGE,"E12")}),1.0]])]});
            var Q1;
            Q1=makeQuery(id+"F0.imprint","IMPRINT",FACE,{"disambiguationData":[TD([[makeQuery(id+"F0.imprint","IMPRINT",EDGE,{"derivedFrom":sQuery(id+"F0.wireOp",EDGE,"E26")}),1.0]])]});
            var Q2;
            Q2=makeQuery(id+"F0.imprint","IMPRINT",FACE,{"disambiguationData":[TD([[makeQuery(id+"F0.imprint","IMPRINT",EDGE,{"derivedFrom":sQuery(id+"F0.wireOp",EDGE,"E506")}),1.0]])]});
            var Q3;
            Q3=makeQuery(id+"F0.imprint","IMPRINT",FACE,{"disambiguationData":[TD([[makeQuery(id+"F0.imprint","IMPRINT",EDGE,{"derivedFrom":sQuery(id+"F0.wireOp",EDGE,"E28")}),1.0]])]});
            extrude(context, id + "F1", {"entities" : qUnion([Q0, Q1, Q2, Q3]), "depth" : 3 * mm, "offsetDistance" : 25 * mm});
        }
        {
            var Q0;
            Q0=makeQuery(id+"F1.opExtrude","CAP_FACE",FACE,{"disambiguationData":[OSD([sQuery(id+"F0.wireOp",EDGE,"E12"),sQuery(id+"F0.wireOp",EDGE,"E13"),sQuery(id+"F0.wireOp",EDGE,"E14"),sQuery(id+"F0.wireOp",EDGE,"E15"),sQuery(id+"F0.wireOp",EDGE,"E16"),sQuery(id+"F0.wireOp",EDGE,"E17"),sQuery(id+"F0.wireOp",EDGE,"E18"),sQuery(id+"F0.wireOp",EDGE,"E19"),sQuery(id+"F0.wireOp",EDGE,"E20"),sQuery(id+"F0.wireOp",EDGE,"E21"),sQuery(id+"F0.wireOp",EDGE,"E22"),sQuery(id+"F0.wireOp",EDGE,"E23"),sQuery(id+"F0.wireOp",EDGE,"E24"),sQuery(id+"F0.wireOp",EDGE,"E25"),sQuery(id+"F0.wireOp",EDGE,"E233"),sQuery(id+"F0.wireOp",EDGE,"E234"),sQuery(id+"F0.wireOp",EDGE,"E235"),sQuery(id+"F0.wireOp",EDGE,"E236"),sQuery(id+"F0.wireOp",EDGE,"E237"),sQuery(id+"F0.wireOp",EDGE,"E238"),sQuery(id+"F0.wireOp",EDGE,"E239"),sQuery(id+"F0.wireOp",EDGE,"E240"),sQuery(id+"F0.wireOp",EDGE,"E241"),sQuery(id+"F0.wireOp",EDGE,"E242"),sQuery(id+"F0.wireOp",EDGE,"E243"),sQuery(id+"F0.wireOp",EDGE,"E244"),sQuery(id+"F0.wireOp",EDGE,"E245"),sQuery(id+"F0.wireOp",EDGE,"E246"),sQuery(id+"F0.wireOp",EDGE,"E247"),sQuery(id+"F0.wireOp",EDGE,"E248"),sQuery(id+"F0.wireOp",EDGE,"E249"),sQuery(id+"F0.wireOp",EDGE,"E250"),sQuery(id+"F0.wireOp",EDGE,"E251"),sQuery(id+"F0.wireOp",EDGE,"E252"),sQuery(id+"F0.wireOp",EDGE,"E253"),sQuery(id+"F0.wireOp",EDGE,"E254"),sQuery(id+"F0.wireOp",EDGE,"E255"),sQuery(id+"F0.wireOp",EDGE,"E256"),sQuery(id+"F0.wireOp",EDGE,"E257"),sQuery(id+"F0.wireOp",EDGE,"E258"),sQuery(id+"F0.wireOp",EDGE,"E259"),sQuery(id+"F0.wireOp",EDGE,"E260"),sQuery(id+"F0.wireOp",EDGE,"E261"),sQuery(id+"F0.wireOp",EDGE,"E262"),sQuery(id+"F0.wireOp",EDGE,"E263"),sQuery(id+"F0.wireOp",EDGE,"E264"),sQuery(id+"F0.wireOp",EDGE,"E265"),sQuery(id+"F0.wireOp",EDGE,"E266"),sQuery(id+"F0.wireOp",EDGE,"E267"),sQuery(id+"F0.wireOp",EDGE,"E268"),sQuery(id+"F0.wireOp",EDGE,"E269"),sQuery(id+"F0.wireOp",EDGE,"E270"),sQuery(id+"F0.wireOp",EDGE,"E271"),sQuery(id+"F0.wireOp",EDGE,"E272"),sQuery(id+"F0.wireOp",EDGE,"E273"),sQuery(id+"F0.wireOp",EDGE,"E274"),sQuery(id+"F0.wireOp",EDGE,"E275"),sQuery(id+"F0.wireOp",EDGE,"E276"),sQuery(id+"F0.wireOp",EDGE,"E277"),sQuery(id+"F0.wireOp",EDGE,"E278"),sQuery(id+"F0.wireOp",EDGE,"E279"),sQuery(id+"F0.wireOp",EDGE,"E280"),sQuery(id+"F0.wireOp",EDGE,"E281"),sQuery(id+"F0.wireOp",EDGE,"E282"),sQuery(id+"F0.wireOp",EDGE,"E283"),sQuery(id+"F0.wireOp",EDGE,"E284"),sQuery(id+"F0.wireOp",EDGE,"E285"),sQuery(id+"F0.wireOp",EDGE,"E286"),sQuery(id+"F0.wireOp",EDGE,"E287"),sQuery(id+"F0.wireOp",EDGE,"E288"),sQuery(id+"F0.wireOp",EDGE,"E289"),sQuery(id+"F0.wireOp",EDGE,"E290"),sQuery(id+"F0.wireOp",EDGE,"E291"),sQuery(id+"F0.wireOp",EDGE,"E292"),sQuery(id+"F0.wireOp",EDGE,"E293"),sQuery(id+"F0.wireOp",EDGE,"E294"),sQuery(id+"F0.wireOp",EDGE,"E295"),sQuery(id+"F0.wireOp",EDGE,"E296"),sQuery(id+"F0.wireOp",EDGE,"E297"),sQuery(id+"F0.wireOp",EDGE,"E298"),sQuery(id+"F0.wireOp",EDGE,"E299"),sQuery(id+"F0.wireOp",EDGE,"E300"),sQuery(id+"F0.wireOp",EDGE,"E301"),sQuery(id+"F0.wireOp",EDGE,"E302"),sQuery(id+"F0.wireOp",EDGE,"E303"),sQuery(id+"F0.wireOp",EDGE,"E304"),sQuery(id+"F0.wireOp",EDGE,"E305"),sQuery(id+"F0.wireOp",EDGE,"E306"),sQuery(id+"F0.wireOp",EDGE,"E307"),sQuery(id+"F0.wireOp",EDGE,"E308"),sQuery(id+"F0.wireOp",EDGE,"E309"),sQuery(id+"F0.wireOp",EDGE,"E310"),sQuery(id+"F0.wireOp",EDGE,"E311"),sQuery(id+"F0.wireOp",EDGE,"E312"),sQuery(id+"F0.wireOp",EDGE,"E313"),sQuery(id+"F0.wireOp",EDGE,"E314"),sQuery(id+"F0.wireOp",EDGE,"E315"),sQuery(id+"F0.wireOp",EDGE,"E316"),sQuery(id+"F0.wireOp",EDGE,"E317"),sQuery(id+"F0.wireOp",EDGE,"E318"),sQuery(id+"F0.wireOp",EDGE,"E319"),sQuery(id+"F0.wireOp",EDGE,"E320"),sQuery(id+"F0.wireOp",EDGE,"E321"),sQuery(id+"F0.wireOp",EDGE,"E322"),sQuery(id+"F0.wireOp",EDGE,"E323"),sQuery(id+"F0.wireOp",EDGE,"E324"),sQuery(id+"F0.wireOp",EDGE,"E325"),sQuery(id+"F0.wireOp",EDGE,"E326"),sQuery(id+"F0.wireOp",EDGE,"E327"),sQuery(id+"F0.wireOp",EDGE,"E328"),sQuery(id+"F0.wireOp",EDGE,"E329"),sQuery(id+"F0.wireOp",EDGE,"E330"),sQuery(id+"F0.wireOp",EDGE,"E331"),sQuery(id+"F0.wireOp",EDGE,"E332"),sQuery(id+"F0.wireOp",EDGE,"E333"),sQuery(id+"F0.wireOp",EDGE,"E334"),sQuery(id+"F0.wireOp",EDGE,"E335"),sQuery(id+"F0.wireOp",EDGE,"E336"),sQuery(id+"F0.wireOp",EDGE,"E337"),sQuery(id+"F0.wireOp",EDGE,"E338"),sQuery(id+"F0.wireOp",EDGE,"E339"),sQuery(id+"F0.wireOp",EDGE,"E340"),sQuery(id+"F0.wireOp",EDGE,"E341"),sQuery(id+"F0.wireOp",EDGE,"E342"),sQuery(id+"F0.wireOp",EDGE,"E343"),sQuery(id+"F0.wireOp",EDGE,"E344"),sQuery(id+"F0.wireOp",EDGE,"E345"),sQuery(id+"F0.wireOp",EDGE,"E346"),sQuery(id+"F0.wireOp",EDGE,"E347"),sQuery(id+"F0.wireOp",EDGE,"E348"),sQuery(id+"F0.wireOp",EDGE,"E349"),sQuery(id+"F0.wireOp",EDGE,"E350"),sQuery(id+"F0.wireOp",EDGE,"E351"),sQuery(id+"F0.wireOp",EDGE,"E352"),sQuery(id+"F0.wireOp",EDGE,"E353"),sQuery(id+"F0.wireOp",EDGE,"E354"),sQuery(id+"F0.wireOp",EDGE,"E355"),sQuery(id+"F0.wireOp",EDGE,"E356"),sQuery(id+"F0.wireOp",EDGE,"E357"),sQuery(id+"F0.wireOp",EDGE,"E358"),sQuery(id+"F0.wireOp",EDGE,"E359"),sQuery(id+"F0.wireOp",EDGE,"E360"),sQuery(id+"F0.wireOp",EDGE,"E361"),sQuery(id+"F0.wireOp",EDGE,"E362"),sQuery(id+"F0.wireOp",EDGE,"E363"),sQuery(id+"F0.wireOp",EDGE,"E364"),sQuery(id+"F0.wireOp",EDGE,"E365"),sQuery(id+"F0.wireOp",EDGE,"E366"),sQuery(id+"F0.wireOp",EDGE,"E367"),sQuery(id+"F0.wireOp",EDGE,"E368"),sQuery(id+"F0.wireOp",EDGE,"E369"),sQuery(id+"F0.wireOp",EDGE,"E370"),sQuery(id+"F0.wireOp",EDGE,"E371"),sQuery(id+"F0.wireOp",EDGE,"E372"),sQuery(id+"F0.wireOp",EDGE,"E373"),sQuery(id+"F0.wireOp",EDGE,"E374"),sQuery(id+"F0.wireOp",EDGE,"E375"),sQuery(id+"F0.wireOp",EDGE,"E376"),sQuery(id+"F0.wireOp",EDGE,"E377"),sQuery(id+"F0.wireOp",EDGE,"E378"),sQuery(id+"F0.wireOp",EDGE,"E379"),sQuery(id+"F0.wireOp",EDGE,"E380"),sQuery(id+"F0.wireOp",EDGE,"E381"),sQuery(id+"F0.wireOp",EDGE,"E382"),sQuery(id+"F0.wireOp",EDGE,"E383"),sQuery(id+"F0.wireOp",EDGE,"E384"),sQuery(id+"F0.wireOp",EDGE,"E385"),sQuery(id+"F0.wireOp",EDGE,"E386"),sQuery(id+"F0.wireOp",EDGE,"E387"),sQuery(id+"F0.wireOp",EDGE,"E388"),sQuery(id+"F0.wireOp",EDGE,"E389"),sQuery(id+"F0.wireOp",EDGE,"E390"),sQuery(id+"F0.wireOp",EDGE,"E391"),sQuery(id+"F0.wireOp",EDGE,"E392"),sQuery(id+"F0.wireOp",EDGE,"E393"),sQuery(id+"F0.wireOp",EDGE,"E394"),sQuery(id+"F0.wireOp",EDGE,"E395"),sQuery(id+"F0.wireOp",EDGE,"E396"),sQuery(id+"F0.wireOp",EDGE,"E397"),sQuery(id+"F0.wireOp",EDGE,"E398"),sQuery(id+"F0.wireOp",EDGE,"E399"),sQuery(id+"F0.wireOp",EDGE,"E400"),sQuery(id+"F0.wireOp",EDGE,"E401"),sQuery(id+"F0.wireOp",EDGE,"E402"),sQuery(id+"F0.wireOp",EDGE,"E403"),sQuery(id+"F0.wireOp",EDGE,"E404"),sQuery(id+"F0.wireOp",EDGE,"E405"),sQuery(id+"F0.wireOp",EDGE,"E406"),sQuery(id+"F0.wireOp",EDGE,"E407"),sQuery(id+"F0.wireOp",EDGE,"E408"),sQuery(id+"F0.wireOp",EDGE,"E409"),sQuery(id+"F0.wireOp",EDGE,"E410"),sQuery(id+"F0.wireOp",EDGE,"E411"),sQuery(id+"F0.wireOp",EDGE,"E412"),sQuery(id+"F0.wireOp",EDGE,"E413"),sQuery(id+"F0.wireOp",EDGE,"E414"),sQuery(id+"F0.wireOp",EDGE,"E415"),sQuery(id+"F0.wireOp",EDGE,"E416"),sQuery(id+"F0.wireOp",EDGE,"E417"),sQuery(id+"F0.wireOp",EDGE,"E418"),sQuery(id+"F0.wireOp",EDGE,"E419"),sQuery(id+"F0.wireOp",EDGE,"E420"),sQuery(id+"F0.wireOp",EDGE,"E421"),sQuery(id+"F0.wireOp",EDGE,"E422"),sQuery(id+"F0.wireOp",EDGE,"E423"),sQuery(id+"F0.wireOp",EDGE,"E424"),sQuery(id+"F0.wireOp",EDGE,"E425"),sQuery(id+"F0.wireOp",EDGE,"E426"),sQuery(id+"F0.wireOp",EDGE,"E427"),sQuery(id+"F0.wireOp",EDGE,"E428"),sQuery(id+"F0.wireOp",EDGE,"E429"),sQuery(id+"F0.wireOp",EDGE,"E430"),sQuery(id+"F0.wireOp",EDGE,"E431"),sQuery(id+"F0.wireOp",EDGE,"E432"),sQuery(id+"F0.wireOp",EDGE,"E433"),sQuery(id+"F0.wireOp",EDGE,"E434"),sQuery(id+"F0.wireOp",EDGE,"E435"),sQuery(id+"F0.wireOp",EDGE,"E436"),sQuery(id+"F0.wireOp",EDGE,"E437"),sQuery(id+"F0.wireOp",EDGE,"E438"),sQuery(id+"F0.wireOp",EDGE,"E439"),sQuery(id+"F0.wireOp",EDGE,"E440"),sQuery(id+"F0.wireOp",EDGE,"E441"),sQuery(id+"F0.wireOp",EDGE,"E442")])],"isStart":false});
            var sketch = newSketch(context, id + "F2", { "sketchPlane" : qUnion([Q0])});
            skLineSegment(sketch, "E526", {"start": v(-18.12, 52.26) * mm, "end": v(-2.72, 52.26) * mm});
            skLineSegment(sketch, "E527", {"start": v(-2.72, 52.26) * mm, "end": v(-2.72, 57.25) * mm});
            skLineSegment(sketch, "E528", {"start": v(-2.72, 57.25) * mm, "end": v(9.81, 57.25) * mm});
            skLineSegment(sketch, "E529", {"start": v(9.81, 57.25) * mm, "end": v(9.81, 54.32) * mm});
            skLineSegment(sketch, "E530", {"start": v(9.81, 54.32) * mm, "end": v(15.66, 54.32) * mm});
            skLineSegment(sketch, "E531", {"start": v(15.66, 54.32) * mm, "end": v(15.66, 46.72) * mm});
            skLineSegment(sketch, "E532", {"start": v(15.66, 46.72) * mm, "end": v(7.64, 37.18) * mm});
            skLineSegment(sketch, "E533", {"start": v(7.64, 37.18) * mm, "end": v(-2.52, 37.18) * mm});
            skLineSegment(sketch, "E534", {"start": v(-2.52, 37.18) * mm, "end": v(-2.52, 39.55) * mm});
            skLineSegment(sketch, "E535", {"start": v(-2.52, 39.55) * mm, "end": v(-24.5, 39.55) * mm});
            skLineSegment(sketch, "E536", {"start": v(15.66, 51.29) * mm, "end": v(21.38, 51.29) * mm});
            skLineSegment(sketch, "E537", {"start": v(21.38, 51.29) * mm, "end": v(21.38, 60.62) * mm});
            skLineSegment(sketch, "E538", {"start": v(7.64, 37.18) * mm, "end": v(7.64, 29.75) * mm});
            skLineSegment(sketch, "E539", {"start": v(7.64, 29.75) * mm, "end": v(12.1, 22.91) * mm});
            skLineSegment(sketch, "E540", {"start": v(12.1, 22.91) * mm, "end": v(27.69, 22.91) * mm});
            skLineSegment(sketch, "E541", {"start": v(12.1, 22.91) * mm, "end": v(12.1, 16.76) * mm});
            skLineSegment(sketch, "E542", {"start": v(12.1, 16.76) * mm, "end": v(1.97, 16.76) * mm});
            skLineSegment(sketch, "E543", {"start": v(1.97, 16.76) * mm, "end": v(-2.49, 11.93) * mm});
            skLineSegment(sketch, "E544", {"start": v(-2.49, 11.93) * mm, "end": v(-2.49, -5.73) * mm});
            skLineSegment(sketch, "E545", {"start": v(-2.49, -5.73) * mm, "end": v(-11.22, -5.73) * mm});
            skLineSegment(sketch, "E546", {"start": v(-11.22, -5.73) * mm, "end": v(-11.22, -20.41) * mm});
            skLineSegment(sketch, "E547", {"start": v(-11.22, -20.41) * mm, "end": v(-37.41, -20.41) * mm});
            skLineSegment(sketch, "E548", {"start": v(12.1, 16.76) * mm, "end": v(12.1, 6.9) * mm});
            skLineSegment(sketch, "E549", {"start": v(12.1, 6.9) * mm, "end": v(20, 4.1) * mm});
            skLineSegment(sketch, "E550", {"start": v(20, 4.1) * mm, "end": v(21.49, 1.6) * mm});
            skLineSegment(sketch, "E551", {"start": v(21.49, 1.6) * mm, "end": v(30.51, 5.43) * mm});
            skSolve(sketch);
        }
        {
            var Q0;
            Q0=makeQuery(id+"F2.imprint","IMPRINT",FACE,{"disambiguationData":[TD([[makeQuery(id+"F2.imprint","IMPRINT",EDGE,{"derivedFrom":sQuery(id+"F2.wireOp",EDGE,"E526")}),1.0]])]});
            var Q1;
            Q1=makeQuery(id+"F2.imprint","IMPRINT",FACE,{"disambiguationData":[TD([[makeQuery(id+"F2.imprint","IMPRINT",EDGE,{"derivedFrom":sQuery(id+"F2.wireOp",EDGE,"E526")}),-1.0]])]});
            var Q2;
            {var subQ3=sQuery(id+"F2.wireOp",EDGE,"E532");Q2=makeQuery(id+"F2.imprint","IMPRINT",FACE,{"disambiguationData":[TD([[makeQuery(id+"F2.imprint","IMPRINT",EDGE,{"derivedFrom":subQ3}),1.0]])]});}
            var Q3;
            {var subQ2=sQuery(id+"F2.wireOp",EDGE,"E540");Q3=makeQuery(id+"F2.imprint","IMPRINT",FACE,{"disambiguationData":[TD([[makeQuery(id+"F2.imprint","IMPRINT",EDGE,{"derivedFrom":subQ2}),-1.0]])]});}
            var Q4;
            Q4=makeQuery(id+"F2.imprint","IMPRINT",FACE,{"disambiguationData":[TD([[makeQuery(id+"F2.imprint","IMPRINT",EDGE,{"derivedFrom":sQuery(id+"F2.wireOp",EDGE,"E542")}),1.0]])]});
            extrude(context, id + "F3", {"entities" : qUnion([Q0, Q1, Q2, Q3, Q4]), "operationType" : NewBodyOperationType.REMOVE, "oppositeDirection" : true, "depth" : 25 * mm, "offsetDistance" : 25 * mm});
        }
    });
